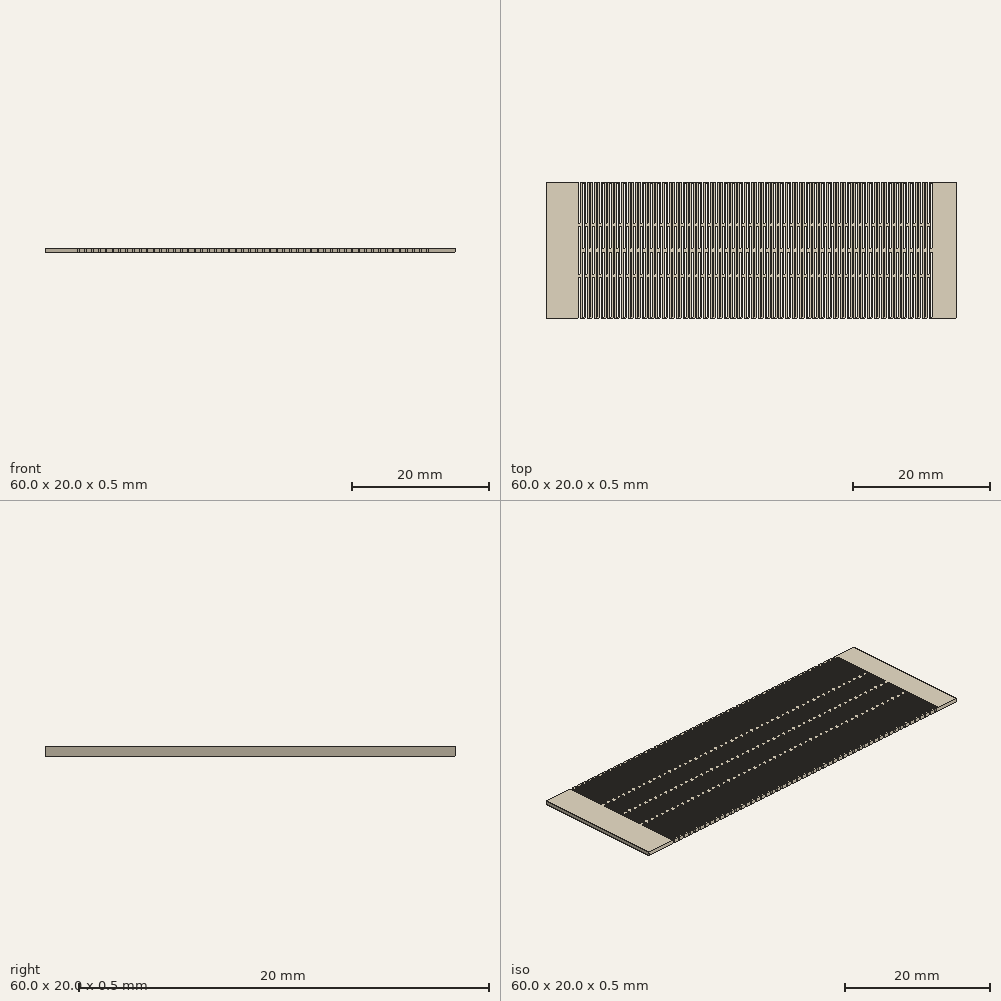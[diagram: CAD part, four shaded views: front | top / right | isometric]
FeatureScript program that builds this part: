
annotation { "Feature Type Name" : "Feature", "Feature Type Description" : "" }
export const myFeature = defineFeature(function(context is Context, id is Id, definition is map)
    precondition{}
    {
        {
            var Q0;
            Q0=qCreatedBy(makeId("Top.planeOp"),FACE);
            var sketch = newSketch(context, id + "F0", { "sketchPlane" : qUnion([Q0])});
            skLineSegment(sketch, "E0.bottom", {"start": v(30, -10) * mm, "end": v(-25, -10) * mm});
            skLineSegment(sketch, "E0.top", {"start": v(30, 10) * mm, "end": v(-24, 10) * mm});
            skLineSegment(sketch, "E0.left", {"start": v(30, -10) * mm, "end": v(30, 10) * mm});
            skLineSegment(sketch, "E0.right", {"start": v(-30, -10) * mm, "end": v(-30, 10) * mm});
            skPoint(sketch, "E0.middle", {"position": v(0, 0) * mm});
            skLineSegment(sketch, "E1", {"start": v(-25.25, 10) * mm, "end": v(-25.25, 4) * mm});
            skLineSegment(sketch, "E2", {"start": v(-25.25, 4) * mm, "end": v(-25, 4) * mm});
            skLineSegment(sketch, "E3", {"start": v(-25, 4) * mm, "end": v(-25, 10) * mm});
            skLineSegment(sketch, "E4", {"start": v(-25, 0) * mm, "end": v(-25, 3.5) * mm});
            skLineSegment(sketch, "E5", {"start": v(-25, 3.5) * mm, "end": v(-25.25, 3.5) * mm});
            skLineSegment(sketch, "E6", {"start": v(-25.25, 3.5) * mm, "end": v(-25.25, 0) * mm});
            skLineSegment(sketch, "E7", {"start": v(-24.75, 9.75) * mm, "end": v(-24.5, 9.75) * mm});
            skLineSegment(sketch, "E8", {"start": v(-24.5, 9.75) * mm, "end": v(-24.5, 0.25) * mm});
            skLineSegment(sketch, "E9", {"start": v(-24.5, 0.25) * mm, "end": v(-24.75, 0.25) * mm});
            skLineSegment(sketch, "E10", {"start": v(-24.75, 0.25) * mm, "end": v(-24.75, 9.75) * mm});
            skLineSegment(sketch, "E11.trimOffspring", {"start": v(-25.25, 10) * mm, "end": v(-30, 10) * mm});
            skLineSegment(sketch, "E12.MirrorCS", {"start": v(-25, 0) * mm, "end": v(-25, -3.5) * mm});
            skLineSegment(sketch, "E13.MirrorCS", {"start": v(-25, -3.5) * mm, "end": v(-25.25, -3.5) * mm});
            skLineSegment(sketch, "E14.MirrorCS", {"start": v(-25.25, -3.5) * mm, "end": v(-25.25, 0) * mm});
            skLineSegment(sketch, "E15.MirrorCS", {"start": v(-24.5, -0.25) * mm, "end": v(-24.75, -0.25) * mm});
            skLineSegment(sketch, "E16.MirrorCS", {"start": v(-24.75, -9.75) * mm, "end": v(-24.5, -9.75) * mm});
            skLineSegment(sketch, "E17.MirrorCS", {"start": v(-24.5, -9.75) * mm, "end": v(-24.5, -0.25) * mm});
            skLineSegment(sketch, "E18.MirrorCS", {"start": v(-24.75, -0.25) * mm, "end": v(-24.75, -9.75) * mm});
            skLineSegment(sketch, "E19.MirrorCS", {"start": v(-25, -4) * mm, "end": v(-25, -10) * mm});
            skLineSegment(sketch, "E20.MirrorCS", {"start": v(-25.25, -10) * mm, "end": v(-25.25, -4) * mm});
            skLineSegment(sketch, "E21.MirrorCS", {"start": v(-25.25, -4) * mm, "end": v(-25, -4) * mm});
            skLineSegment(sketch, "E22.trimOffspring", {"start": v(-25.25, -10) * mm, "end": v(-30, -10) * mm});
            skLineSegment(sketch, "E23.1.0.0", {"start": v(-24.25, 10) * mm, "end": v(-24.25, 4) * mm});
            skLineSegment(sketch, "E23.1.0.1", {"start": v(-24, 4) * mm, "end": v(-24, 10) * mm});
            skLineSegment(sketch, "E23.1.0.2", {"start": v(-23.75, 0.25) * mm, "end": v(-23.75, 9.75) * mm});
            skLineSegment(sketch, "E23.1.0.3", {"start": v(-23.5, 9.75) * mm, "end": v(-23.5, 0.25) * mm});
            skLineSegment(sketch, "E23.1.0.4", {"start": v(-23.75, 9.75) * mm, "end": v(-23.5, 9.75) * mm});
            skLineSegment(sketch, "E23.1.0.5", {"start": v(-24.25, 4) * mm, "end": v(-24, 4) * mm});
            skLineSegment(sketch, "E23.1.0.6", {"start": v(-23.5, 0.25) * mm, "end": v(-23.75, 0.25) * mm});
            skLineSegment(sketch, "E23.1.0.7", {"start": v(-24.25, 3.5) * mm, "end": v(-24.25, 0) * mm});
            skLineSegment(sketch, "E23.1.0.8", {"start": v(-24, 3.5) * mm, "end": v(-24.25, 3.5) * mm});
            skLineSegment(sketch, "E23.1.0.9", {"start": v(-24, 0) * mm, "end": v(-24, 3.5) * mm});
            skLineSegment(sketch, "E23.1.0.10", {"start": v(-24.25, -3.5) * mm, "end": v(-24.25, 0) * mm});
            skLineSegment(sketch, "E23.1.0.11", {"start": v(-24, -3.5) * mm, "end": v(-24.25, -3.5) * mm});
            skLineSegment(sketch, "E23.1.0.12", {"start": v(-24, 0) * mm, "end": v(-24, -3.5) * mm});
            skLineSegment(sketch, "E23.1.0.13", {"start": v(-23.75, -0.25) * mm, "end": v(-23.75, -9.75) * mm});
            skLineSegment(sketch, "E23.1.0.14", {"start": v(-23.5, -0.25) * mm, "end": v(-23.75, -0.25) * mm});
            skLineSegment(sketch, "E23.1.0.15", {"start": v(-23.5, -9.75) * mm, "end": v(-23.5, -0.25) * mm});
            skLineSegment(sketch, "E23.1.0.16", {"start": v(-23.75, -9.75) * mm, "end": v(-23.5, -9.75) * mm});
            skLineSegment(sketch, "E23.1.0.17", {"start": v(-24, -4) * mm, "end": v(-24, -10) * mm});
            skLineSegment(sketch, "E23.1.0.18", {"start": v(-24.25, -10) * mm, "end": v(-24.25, -4) * mm});
            skLineSegment(sketch, "E23.1.0.19", {"start": v(-24.25, -4) * mm, "end": v(-24, -4) * mm});
            skLineSegment(sketch, "E23.2.0.0", {"start": v(-23.25, 10) * mm, "end": v(-23.25, 4) * mm});
            skLineSegment(sketch, "E23.2.0.1", {"start": v(-23, 4) * mm, "end": v(-23, 10) * mm});
            skLineSegment(sketch, "E23.2.0.2", {"start": v(-22.75, 0.25) * mm, "end": v(-22.75, 9.75) * mm});
            skLineSegment(sketch, "E23.2.0.3", {"start": v(-22.5, 9.75) * mm, "end": v(-22.5, 0.25) * mm});
            skLineSegment(sketch, "E23.2.0.4", {"start": v(-22.75, 9.75) * mm, "end": v(-22.5, 9.75) * mm});
            skLineSegment(sketch, "E23.2.0.5", {"start": v(-23.25, 4) * mm, "end": v(-23, 4) * mm});
            skLineSegment(sketch, "E23.2.0.6", {"start": v(-22.5, 0.25) * mm, "end": v(-22.75, 0.25) * mm});
            skLineSegment(sketch, "E23.2.0.7", {"start": v(-23.25, 3.5) * mm, "end": v(-23.25, 0) * mm});
            skLineSegment(sketch, "E23.2.0.8", {"start": v(-23, 3.5) * mm, "end": v(-23.25, 3.5) * mm});
            skLineSegment(sketch, "E23.2.0.9", {"start": v(-23, 0) * mm, "end": v(-23, 3.5) * mm});
            skLineSegment(sketch, "E23.2.0.10", {"start": v(-23.25, -3.5) * mm, "end": v(-23.25, 0) * mm});
            skLineSegment(sketch, "E23.2.0.11", {"start": v(-23, -3.5) * mm, "end": v(-23.25, -3.5) * mm});
            skLineSegment(sketch, "E23.2.0.12", {"start": v(-23, 0) * mm, "end": v(-23, -3.5) * mm});
            skLineSegment(sketch, "E23.2.0.13", {"start": v(-22.75, -0.25) * mm, "end": v(-22.75, -9.75) * mm});
            skLineSegment(sketch, "E23.2.0.14", {"start": v(-22.5, -0.25) * mm, "end": v(-22.75, -0.25) * mm});
            skLineSegment(sketch, "E23.2.0.15", {"start": v(-22.5, -9.75) * mm, "end": v(-22.5, -0.25) * mm});
            skLineSegment(sketch, "E23.2.0.16", {"start": v(-22.75, -9.75) * mm, "end": v(-22.5, -9.75) * mm});
            skLineSegment(sketch, "E23.2.0.17", {"start": v(-23, -4) * mm, "end": v(-23, -10) * mm});
            skLineSegment(sketch, "E23.2.0.18", {"start": v(-23.25, -10) * mm, "end": v(-23.25, -4) * mm});
            skLineSegment(sketch, "E23.2.0.19", {"start": v(-23.25, -4) * mm, "end": v(-23, -4) * mm});
            skLineSegment(sketch, "E23.3.0.0", {"start": v(-22.25, 10) * mm, "end": v(-22.25, 4) * mm});
            skLineSegment(sketch, "E23.3.0.1", {"start": v(-22, 4) * mm, "end": v(-22, 10) * mm});
            skLineSegment(sketch, "E23.3.0.2", {"start": v(-21.75, 0.25) * mm, "end": v(-21.75, 9.75) * mm});
            skLineSegment(sketch, "E23.3.0.3", {"start": v(-21.5, 9.75) * mm, "end": v(-21.5, 0.25) * mm});
            skLineSegment(sketch, "E23.3.0.4", {"start": v(-21.75, 9.75) * mm, "end": v(-21.5, 9.75) * mm});
            skLineSegment(sketch, "E23.3.0.5", {"start": v(-22.25, 4) * mm, "end": v(-22, 4) * mm});
            skLineSegment(sketch, "E23.3.0.6", {"start": v(-21.5, 0.25) * mm, "end": v(-21.75, 0.25) * mm});
            skLineSegment(sketch, "E23.3.0.7", {"start": v(-22.25, 3.5) * mm, "end": v(-22.25, 0) * mm});
            skLineSegment(sketch, "E23.3.0.8", {"start": v(-22, 3.5) * mm, "end": v(-22.25, 3.5) * mm});
            skLineSegment(sketch, "E23.3.0.9", {"start": v(-22, 0) * mm, "end": v(-22, 3.5) * mm});
            skLineSegment(sketch, "E23.3.0.10", {"start": v(-22.25, -3.5) * mm, "end": v(-22.25, 0) * mm});
            skLineSegment(sketch, "E23.3.0.11", {"start": v(-22, -3.5) * mm, "end": v(-22.25, -3.5) * mm});
            skLineSegment(sketch, "E23.3.0.12", {"start": v(-22, 0) * mm, "end": v(-22, -3.5) * mm});
            skLineSegment(sketch, "E23.3.0.13", {"start": v(-21.75, -0.25) * mm, "end": v(-21.75, -9.75) * mm});
            skLineSegment(sketch, "E23.3.0.14", {"start": v(-21.5, -0.25) * mm, "end": v(-21.75, -0.25) * mm});
            skLineSegment(sketch, "E23.3.0.15", {"start": v(-21.5, -9.75) * mm, "end": v(-21.5, -0.25) * mm});
            skLineSegment(sketch, "E23.3.0.16", {"start": v(-21.75, -9.75) * mm, "end": v(-21.5, -9.75) * mm});
            skLineSegment(sketch, "E23.3.0.17", {"start": v(-22, -4) * mm, "end": v(-22, -10) * mm});
            skLineSegment(sketch, "E23.3.0.18", {"start": v(-22.25, -10) * mm, "end": v(-22.25, -4) * mm});
            skLineSegment(sketch, "E23.3.0.19", {"start": v(-22.25, -4) * mm, "end": v(-22, -4) * mm});
            skLineSegment(sketch, "E23.4.0.0", {"start": v(-21.25, 10) * mm, "end": v(-21.25, 4) * mm});
            skLineSegment(sketch, "E23.4.0.1", {"start": v(-21, 4) * mm, "end": v(-21, 10) * mm});
            skLineSegment(sketch, "E23.4.0.2", {"start": v(-20.75, 0.25) * mm, "end": v(-20.75, 9.75) * mm});
            skLineSegment(sketch, "E23.4.0.3", {"start": v(-20.5, 9.75) * mm, "end": v(-20.5, 0.25) * mm});
            skLineSegment(sketch, "E23.4.0.4", {"start": v(-20.75, 9.75) * mm, "end": v(-20.5, 9.75) * mm});
            skLineSegment(sketch, "E23.4.0.5", {"start": v(-21.25, 4) * mm, "end": v(-21, 4) * mm});
            skLineSegment(sketch, "E23.4.0.6", {"start": v(-20.5, 0.25) * mm, "end": v(-20.75, 0.25) * mm});
            skLineSegment(sketch, "E23.4.0.7", {"start": v(-21.25, 3.5) * mm, "end": v(-21.25, 0) * mm});
            skLineSegment(sketch, "E23.4.0.8", {"start": v(-21, 3.5) * mm, "end": v(-21.25, 3.5) * mm});
            skLineSegment(sketch, "E23.4.0.9", {"start": v(-21, 0) * mm, "end": v(-21, 3.5) * mm});
            skLineSegment(sketch, "E23.4.0.10", {"start": v(-21.25, -3.5) * mm, "end": v(-21.25, 0) * mm});
            skLineSegment(sketch, "E23.4.0.11", {"start": v(-21, -3.5) * mm, "end": v(-21.25, -3.5) * mm});
            skLineSegment(sketch, "E23.4.0.12", {"start": v(-21, 0) * mm, "end": v(-21, -3.5) * mm});
            skLineSegment(sketch, "E23.4.0.13", {"start": v(-20.75, -0.25) * mm, "end": v(-20.75, -9.75) * mm});
            skLineSegment(sketch, "E23.4.0.14", {"start": v(-20.5, -0.25) * mm, "end": v(-20.75, -0.25) * mm});
            skLineSegment(sketch, "E23.4.0.15", {"start": v(-20.5, -9.75) * mm, "end": v(-20.5, -0.25) * mm});
            skLineSegment(sketch, "E23.4.0.16", {"start": v(-20.75, -9.75) * mm, "end": v(-20.5, -9.75) * mm});
            skLineSegment(sketch, "E23.4.0.17", {"start": v(-21, -4) * mm, "end": v(-21, -10) * mm});
            skLineSegment(sketch, "E23.4.0.18", {"start": v(-21.25, -10) * mm, "end": v(-21.25, -4) * mm});
            skLineSegment(sketch, "E23.4.0.19", {"start": v(-21.25, -4) * mm, "end": v(-21, -4) * mm});
            skLineSegment(sketch, "E23.5.0.0", {"start": v(-20.25, 10) * mm, "end": v(-20.25, 4) * mm});
            skLineSegment(sketch, "E23.5.0.1", {"start": v(-20, 4) * mm, "end": v(-20, 10) * mm});
            skLineSegment(sketch, "E23.5.0.2", {"start": v(-19.75, 0.25) * mm, "end": v(-19.75, 9.75) * mm});
            skLineSegment(sketch, "E23.5.0.3", {"start": v(-19.5, 9.75) * mm, "end": v(-19.5, 0.25) * mm});
            skLineSegment(sketch, "E23.5.0.4", {"start": v(-19.75, 9.75) * mm, "end": v(-19.5, 9.75) * mm});
            skLineSegment(sketch, "E23.5.0.5", {"start": v(-20.25, 4) * mm, "end": v(-20, 4) * mm});
            skLineSegment(sketch, "E23.5.0.6", {"start": v(-19.5, 0.25) * mm, "end": v(-19.75, 0.25) * mm});
            skLineSegment(sketch, "E23.5.0.7", {"start": v(-20.25, 3.5) * mm, "end": v(-20.25, 0) * mm});
            skLineSegment(sketch, "E23.5.0.8", {"start": v(-20, 3.5) * mm, "end": v(-20.25, 3.5) * mm});
            skLineSegment(sketch, "E23.5.0.9", {"start": v(-20, 0) * mm, "end": v(-20, 3.5) * mm});
            skLineSegment(sketch, "E23.5.0.10", {"start": v(-20.25, -3.5) * mm, "end": v(-20.25, 0) * mm});
            skLineSegment(sketch, "E23.5.0.11", {"start": v(-20, -3.5) * mm, "end": v(-20.25, -3.5) * mm});
            skLineSegment(sketch, "E23.5.0.12", {"start": v(-20, 0) * mm, "end": v(-20, -3.5) * mm});
            skLineSegment(sketch, "E23.5.0.13", {"start": v(-19.75, -0.25) * mm, "end": v(-19.75, -9.75) * mm});
            skLineSegment(sketch, "E23.5.0.14", {"start": v(-19.5, -0.25) * mm, "end": v(-19.75, -0.25) * mm});
            skLineSegment(sketch, "E23.5.0.15", {"start": v(-19.5, -9.75) * mm, "end": v(-19.5, -0.25) * mm});
            skLineSegment(sketch, "E23.5.0.16", {"start": v(-19.75, -9.75) * mm, "end": v(-19.5, -9.75) * mm});
            skLineSegment(sketch, "E23.5.0.17", {"start": v(-20, -4) * mm, "end": v(-20, -10) * mm});
            skLineSegment(sketch, "E23.5.0.18", {"start": v(-20.25, -10) * mm, "end": v(-20.25, -4) * mm});
            skLineSegment(sketch, "E23.5.0.19", {"start": v(-20.25, -4) * mm, "end": v(-20, -4) * mm});
            skLineSegment(sketch, "E23.6.0.0", {"start": v(-19.25, 10) * mm, "end": v(-19.25, 4) * mm});
            skLineSegment(sketch, "E23.6.0.1", {"start": v(-19, 4) * mm, "end": v(-19, 10) * mm});
            skLineSegment(sketch, "E23.6.0.2", {"start": v(-18.75, 0.25) * mm, "end": v(-18.75, 9.75) * mm});
            skLineSegment(sketch, "E23.6.0.3", {"start": v(-18.5, 9.75) * mm, "end": v(-18.5, 0.25) * mm});
            skLineSegment(sketch, "E23.6.0.4", {"start": v(-18.75, 9.75) * mm, "end": v(-18.5, 9.75) * mm});
            skLineSegment(sketch, "E23.6.0.5", {"start": v(-19.25, 4) * mm, "end": v(-19, 4) * mm});
            skLineSegment(sketch, "E23.6.0.6", {"start": v(-18.5, 0.25) * mm, "end": v(-18.75, 0.25) * mm});
            skLineSegment(sketch, "E23.6.0.7", {"start": v(-19.25, 3.5) * mm, "end": v(-19.25, 0) * mm});
            skLineSegment(sketch, "E23.6.0.8", {"start": v(-19, 3.5) * mm, "end": v(-19.25, 3.5) * mm});
            skLineSegment(sketch, "E23.6.0.9", {"start": v(-19, 0) * mm, "end": v(-19, 3.5) * mm});
            skLineSegment(sketch, "E23.6.0.10", {"start": v(-19.25, -3.5) * mm, "end": v(-19.25, 0) * mm});
            skLineSegment(sketch, "E23.6.0.11", {"start": v(-19, -3.5) * mm, "end": v(-19.25, -3.5) * mm});
            skLineSegment(sketch, "E23.6.0.12", {"start": v(-19, 0) * mm, "end": v(-19, -3.5) * mm});
            skLineSegment(sketch, "E23.6.0.13", {"start": v(-18.75, -0.25) * mm, "end": v(-18.75, -9.75) * mm});
            skLineSegment(sketch, "E23.6.0.14", {"start": v(-18.5, -0.25) * mm, "end": v(-18.75, -0.25) * mm});
            skLineSegment(sketch, "E23.6.0.15", {"start": v(-18.5, -9.75) * mm, "end": v(-18.5, -0.25) * mm});
            skLineSegment(sketch, "E23.6.0.16", {"start": v(-18.75, -9.75) * mm, "end": v(-18.5, -9.75) * mm});
            skLineSegment(sketch, "E23.6.0.17", {"start": v(-19, -4) * mm, "end": v(-19, -10) * mm});
            skLineSegment(sketch, "E23.6.0.18", {"start": v(-19.25, -10) * mm, "end": v(-19.25, -4) * mm});
            skLineSegment(sketch, "E23.6.0.19", {"start": v(-19.25, -4) * mm, "end": v(-19, -4) * mm});
            skLineSegment(sketch, "E23.7.0.0", {"start": v(-18.25, 10) * mm, "end": v(-18.25, 4) * mm});
            skLineSegment(sketch, "E23.7.0.1", {"start": v(-18, 4) * mm, "end": v(-18, 10) * mm});
            skLineSegment(sketch, "E23.7.0.2", {"start": v(-17.75, 0.25) * mm, "end": v(-17.75, 9.75) * mm});
            skLineSegment(sketch, "E23.7.0.3", {"start": v(-17.5, 9.75) * mm, "end": v(-17.5, 0.25) * mm});
            skLineSegment(sketch, "E23.7.0.4", {"start": v(-17.75, 9.75) * mm, "end": v(-17.5, 9.75) * mm});
            skLineSegment(sketch, "E23.7.0.5", {"start": v(-18.25, 4) * mm, "end": v(-18, 4) * mm});
            skLineSegment(sketch, "E23.7.0.6", {"start": v(-17.5, 0.25) * mm, "end": v(-17.75, 0.25) * mm});
            skLineSegment(sketch, "E23.7.0.7", {"start": v(-18.25, 3.5) * mm, "end": v(-18.25, 0) * mm});
            skLineSegment(sketch, "E23.7.0.8", {"start": v(-18, 3.5) * mm, "end": v(-18.25, 3.5) * mm});
            skLineSegment(sketch, "E23.7.0.9", {"start": v(-18, 0) * mm, "end": v(-18, 3.5) * mm});
            skLineSegment(sketch, "E23.7.0.10", {"start": v(-18.25, -3.5) * mm, "end": v(-18.25, 0) * mm});
            skLineSegment(sketch, "E23.7.0.11", {"start": v(-18, -3.5) * mm, "end": v(-18.25, -3.5) * mm});
            skLineSegment(sketch, "E23.7.0.12", {"start": v(-18, 0) * mm, "end": v(-18, -3.5) * mm});
            skLineSegment(sketch, "E23.7.0.13", {"start": v(-17.75, -0.25) * mm, "end": v(-17.75, -9.75) * mm});
            skLineSegment(sketch, "E23.7.0.14", {"start": v(-17.5, -0.25) * mm, "end": v(-17.75, -0.25) * mm});
            skLineSegment(sketch, "E23.7.0.15", {"start": v(-17.5, -9.75) * mm, "end": v(-17.5, -0.25) * mm});
            skLineSegment(sketch, "E23.7.0.16", {"start": v(-17.75, -9.75) * mm, "end": v(-17.5, -9.75) * mm});
            skLineSegment(sketch, "E23.7.0.17", {"start": v(-18, -4) * mm, "end": v(-18, -10) * mm});
            skLineSegment(sketch, "E23.7.0.18", {"start": v(-18.25, -10) * mm, "end": v(-18.25, -4) * mm});
            skLineSegment(sketch, "E23.7.0.19", {"start": v(-18.25, -4) * mm, "end": v(-18, -4) * mm});
            skLineSegment(sketch, "E23.8.0.0", {"start": v(-17.25, 10) * mm, "end": v(-17.25, 4) * mm});
            skLineSegment(sketch, "E23.8.0.1", {"start": v(-17, 4) * mm, "end": v(-17, 10) * mm});
            skLineSegment(sketch, "E23.8.0.2", {"start": v(-16.75, 0.25) * mm, "end": v(-16.75, 9.75) * mm});
            skLineSegment(sketch, "E23.8.0.3", {"start": v(-16.5, 9.75) * mm, "end": v(-16.5, 0.25) * mm});
            skLineSegment(sketch, "E23.8.0.4", {"start": v(-16.75, 9.75) * mm, "end": v(-16.5, 9.75) * mm});
            skLineSegment(sketch, "E23.8.0.5", {"start": v(-17.25, 4) * mm, "end": v(-17, 4) * mm});
            skLineSegment(sketch, "E23.8.0.6", {"start": v(-16.5, 0.25) * mm, "end": v(-16.75, 0.25) * mm});
            skLineSegment(sketch, "E23.8.0.7", {"start": v(-17.25, 3.5) * mm, "end": v(-17.25, 0) * mm});
            skLineSegment(sketch, "E23.8.0.8", {"start": v(-17, 3.5) * mm, "end": v(-17.25, 3.5) * mm});
            skLineSegment(sketch, "E23.8.0.9", {"start": v(-17, 0) * mm, "end": v(-17, 3.5) * mm});
            skLineSegment(sketch, "E23.8.0.10", {"start": v(-17.25, -3.5) * mm, "end": v(-17.25, 0) * mm});
            skLineSegment(sketch, "E23.8.0.11", {"start": v(-17, -3.5) * mm, "end": v(-17.25, -3.5) * mm});
            skLineSegment(sketch, "E23.8.0.12", {"start": v(-17, 0) * mm, "end": v(-17, -3.5) * mm});
            skLineSegment(sketch, "E23.8.0.13", {"start": v(-16.75, -0.25) * mm, "end": v(-16.75, -9.75) * mm});
            skLineSegment(sketch, "E23.8.0.14", {"start": v(-16.5, -0.25) * mm, "end": v(-16.75, -0.25) * mm});
            skLineSegment(sketch, "E23.8.0.15", {"start": v(-16.5, -9.75) * mm, "end": v(-16.5, -0.25) * mm});
            skLineSegment(sketch, "E23.8.0.16", {"start": v(-16.75, -9.75) * mm, "end": v(-16.5, -9.75) * mm});
            skLineSegment(sketch, "E23.8.0.17", {"start": v(-17, -4) * mm, "end": v(-17, -10) * mm});
            skLineSegment(sketch, "E23.8.0.18", {"start": v(-17.25, -10) * mm, "end": v(-17.25, -4) * mm});
            skLineSegment(sketch, "E23.8.0.19", {"start": v(-17.25, -4) * mm, "end": v(-17, -4) * mm});
            skLineSegment(sketch, "E23.9.0.0", {"start": v(-16.25, 10) * mm, "end": v(-16.25, 4) * mm});
            skLineSegment(sketch, "E23.9.0.1", {"start": v(-16, 4) * mm, "end": v(-16, 10) * mm});
            skLineSegment(sketch, "E23.9.0.2", {"start": v(-15.75, 0.25) * mm, "end": v(-15.75, 9.75) * mm});
            skLineSegment(sketch, "E23.9.0.3", {"start": v(-15.5, 9.75) * mm, "end": v(-15.5, 0.25) * mm});
            skLineSegment(sketch, "E23.9.0.4", {"start": v(-15.75, 9.75) * mm, "end": v(-15.5, 9.75) * mm});
            skLineSegment(sketch, "E23.9.0.5", {"start": v(-16.25, 4) * mm, "end": v(-16, 4) * mm});
            skLineSegment(sketch, "E23.9.0.6", {"start": v(-15.5, 0.25) * mm, "end": v(-15.75, 0.25) * mm});
            skLineSegment(sketch, "E23.9.0.7", {"start": v(-16.25, 3.5) * mm, "end": v(-16.25, 0) * mm});
            skLineSegment(sketch, "E23.9.0.8", {"start": v(-16, 3.5) * mm, "end": v(-16.25, 3.5) * mm});
            skLineSegment(sketch, "E23.9.0.9", {"start": v(-16, 0) * mm, "end": v(-16, 3.5) * mm});
            skLineSegment(sketch, "E23.9.0.10", {"start": v(-16.25, -3.5) * mm, "end": v(-16.25, 0) * mm});
            skLineSegment(sketch, "E23.9.0.11", {"start": v(-16, -3.5) * mm, "end": v(-16.25, -3.5) * mm});
            skLineSegment(sketch, "E23.9.0.12", {"start": v(-16, 0) * mm, "end": v(-16, -3.5) * mm});
            skLineSegment(sketch, "E23.9.0.13", {"start": v(-15.75, -0.25) * mm, "end": v(-15.75, -9.75) * mm});
            skLineSegment(sketch, "E23.9.0.14", {"start": v(-15.5, -0.25) * mm, "end": v(-15.75, -0.25) * mm});
            skLineSegment(sketch, "E23.9.0.15", {"start": v(-15.5, -9.75) * mm, "end": v(-15.5, -0.25) * mm});
            skLineSegment(sketch, "E23.9.0.16", {"start": v(-15.75, -9.75) * mm, "end": v(-15.5, -9.75) * mm});
            skLineSegment(sketch, "E23.9.0.17", {"start": v(-16, -4) * mm, "end": v(-16, -10) * mm});
            skLineSegment(sketch, "E23.9.0.18", {"start": v(-16.25, -10) * mm, "end": v(-16.25, -4) * mm});
            skLineSegment(sketch, "E23.9.0.19", {"start": v(-16.25, -4) * mm, "end": v(-16, -4) * mm});
            skLineSegment(sketch, "E23.10.0.0", {"start": v(-15.25, 10) * mm, "end": v(-15.25, 4) * mm});
            skLineSegment(sketch, "E23.10.0.1", {"start": v(-15, 4) * mm, "end": v(-15, 10) * mm});
            skLineSegment(sketch, "E23.10.0.2", {"start": v(-14.75, 0.25) * mm, "end": v(-14.75, 9.75) * mm});
            skLineSegment(sketch, "E23.10.0.3", {"start": v(-14.5, 9.75) * mm, "end": v(-14.5, 0.25) * mm});
            skLineSegment(sketch, "E23.10.0.4", {"start": v(-14.75, 9.75) * mm, "end": v(-14.5, 9.75) * mm});
            skLineSegment(sketch, "E23.10.0.5", {"start": v(-15.25, 4) * mm, "end": v(-15, 4) * mm});
            skLineSegment(sketch, "E23.10.0.6", {"start": v(-14.5, 0.25) * mm, "end": v(-14.75, 0.25) * mm});
            skLineSegment(sketch, "E23.10.0.7", {"start": v(-15.25, 3.5) * mm, "end": v(-15.25, 0) * mm});
            skLineSegment(sketch, "E23.10.0.8", {"start": v(-15, 3.5) * mm, "end": v(-15.25, 3.5) * mm});
            skLineSegment(sketch, "E23.10.0.9", {"start": v(-15, 0) * mm, "end": v(-15, 3.5) * mm});
            skLineSegment(sketch, "E23.10.0.10", {"start": v(-15.25, -3.5) * mm, "end": v(-15.25, 0) * mm});
            skLineSegment(sketch, "E23.10.0.11", {"start": v(-15, -3.5) * mm, "end": v(-15.25, -3.5) * mm});
            skLineSegment(sketch, "E23.10.0.12", {"start": v(-15, 0) * mm, "end": v(-15, -3.5) * mm});
            skLineSegment(sketch, "E23.10.0.13", {"start": v(-14.75, -0.25) * mm, "end": v(-14.75, -9.75) * mm});
            skLineSegment(sketch, "E23.10.0.14", {"start": v(-14.5, -0.25) * mm, "end": v(-14.75, -0.25) * mm});
            skLineSegment(sketch, "E23.10.0.15", {"start": v(-14.5, -9.75) * mm, "end": v(-14.5, -0.25) * mm});
            skLineSegment(sketch, "E23.10.0.16", {"start": v(-14.75, -9.75) * mm, "end": v(-14.5, -9.75) * mm});
            skLineSegment(sketch, "E23.10.0.17", {"start": v(-15, -4) * mm, "end": v(-15, -10) * mm});
            skLineSegment(sketch, "E23.10.0.18", {"start": v(-15.25, -10) * mm, "end": v(-15.25, -4) * mm});
            skLineSegment(sketch, "E23.10.0.19", {"start": v(-15.25, -4) * mm, "end": v(-15, -4) * mm});
            skLineSegment(sketch, "E23.11.0.0", {"start": v(-14.25, 10) * mm, "end": v(-14.25, 4) * mm});
            skLineSegment(sketch, "E23.11.0.1", {"start": v(-14, 4) * mm, "end": v(-14, 10) * mm});
            skLineSegment(sketch, "E23.11.0.2", {"start": v(-13.75, 0.25) * mm, "end": v(-13.75, 9.75) * mm});
            skLineSegment(sketch, "E23.11.0.3", {"start": v(-13.5, 9.75) * mm, "end": v(-13.5, 0.25) * mm});
            skLineSegment(sketch, "E23.11.0.4", {"start": v(-13.75, 9.75) * mm, "end": v(-13.5, 9.75) * mm});
            skLineSegment(sketch, "E23.11.0.5", {"start": v(-14.25, 4) * mm, "end": v(-14, 4) * mm});
            skLineSegment(sketch, "E23.11.0.6", {"start": v(-13.5, 0.25) * mm, "end": v(-13.75, 0.25) * mm});
            skLineSegment(sketch, "E23.11.0.7", {"start": v(-14.25, 3.5) * mm, "end": v(-14.25, 0) * mm});
            skLineSegment(sketch, "E23.11.0.8", {"start": v(-14, 3.5) * mm, "end": v(-14.25, 3.5) * mm});
            skLineSegment(sketch, "E23.11.0.9", {"start": v(-14, 0) * mm, "end": v(-14, 3.5) * mm});
            skLineSegment(sketch, "E23.11.0.10", {"start": v(-14.25, -3.5) * mm, "end": v(-14.25, 0) * mm});
            skLineSegment(sketch, "E23.11.0.11", {"start": v(-14, -3.5) * mm, "end": v(-14.25, -3.5) * mm});
            skLineSegment(sketch, "E23.11.0.12", {"start": v(-14, 0) * mm, "end": v(-14, -3.5) * mm});
            skLineSegment(sketch, "E23.11.0.13", {"start": v(-13.75, -0.25) * mm, "end": v(-13.75, -9.75) * mm});
            skLineSegment(sketch, "E23.11.0.14", {"start": v(-13.5, -0.25) * mm, "end": v(-13.75, -0.25) * mm});
            skLineSegment(sketch, "E23.11.0.15", {"start": v(-13.5, -9.75) * mm, "end": v(-13.5, -0.25) * mm});
            skLineSegment(sketch, "E23.11.0.16", {"start": v(-13.75, -9.75) * mm, "end": v(-13.5, -9.75) * mm});
            skLineSegment(sketch, "E23.11.0.17", {"start": v(-14, -4) * mm, "end": v(-14, -10) * mm});
            skLineSegment(sketch, "E23.11.0.18", {"start": v(-14.25, -10) * mm, "end": v(-14.25, -4) * mm});
            skLineSegment(sketch, "E23.11.0.19", {"start": v(-14.25, -4) * mm, "end": v(-14, -4) * mm});
            skLineSegment(sketch, "E23.12.0.0", {"start": v(-13.25, 10) * mm, "end": v(-13.25, 4) * mm});
            skLineSegment(sketch, "E23.12.0.1", {"start": v(-13, 4) * mm, "end": v(-13, 10) * mm});
            skLineSegment(sketch, "E23.12.0.2", {"start": v(-12.75, 0.25) * mm, "end": v(-12.75, 9.75) * mm});
            skLineSegment(sketch, "E23.12.0.3", {"start": v(-12.5, 9.75) * mm, "end": v(-12.5, 0.25) * mm});
            skLineSegment(sketch, "E23.12.0.4", {"start": v(-12.75, 9.75) * mm, "end": v(-12.5, 9.75) * mm});
            skLineSegment(sketch, "E23.12.0.5", {"start": v(-13.25, 4) * mm, "end": v(-13, 4) * mm});
            skLineSegment(sketch, "E23.12.0.6", {"start": v(-12.5, 0.25) * mm, "end": v(-12.75, 0.25) * mm});
            skLineSegment(sketch, "E23.12.0.7", {"start": v(-13.25, 3.5) * mm, "end": v(-13.25, 0) * mm});
            skLineSegment(sketch, "E23.12.0.8", {"start": v(-13, 3.5) * mm, "end": v(-13.25, 3.5) * mm});
            skLineSegment(sketch, "E23.12.0.9", {"start": v(-13, 0) * mm, "end": v(-13, 3.5) * mm});
            skLineSegment(sketch, "E23.12.0.10", {"start": v(-13.25, -3.5) * mm, "end": v(-13.25, 0) * mm});
            skLineSegment(sketch, "E23.12.0.11", {"start": v(-13, -3.5) * mm, "end": v(-13.25, -3.5) * mm});
            skLineSegment(sketch, "E23.12.0.12", {"start": v(-13, 0) * mm, "end": v(-13, -3.5) * mm});
            skLineSegment(sketch, "E23.12.0.13", {"start": v(-12.75, -0.25) * mm, "end": v(-12.75, -9.75) * mm});
            skLineSegment(sketch, "E23.12.0.14", {"start": v(-12.5, -0.25) * mm, "end": v(-12.75, -0.25) * mm});
            skLineSegment(sketch, "E23.12.0.15", {"start": v(-12.5, -9.75) * mm, "end": v(-12.5, -0.25) * mm});
            skLineSegment(sketch, "E23.12.0.16", {"start": v(-12.75, -9.75) * mm, "end": v(-12.5, -9.75) * mm});
            skLineSegment(sketch, "E23.12.0.17", {"start": v(-13, -4) * mm, "end": v(-13, -10) * mm});
            skLineSegment(sketch, "E23.12.0.18", {"start": v(-13.25, -10) * mm, "end": v(-13.25, -4) * mm});
            skLineSegment(sketch, "E23.12.0.19", {"start": v(-13.25, -4) * mm, "end": v(-13, -4) * mm});
            skLineSegment(sketch, "E23.13.0.0", {"start": v(-12.25, 10) * mm, "end": v(-12.25, 4) * mm});
            skLineSegment(sketch, "E23.13.0.1", {"start": v(-12, 4) * mm, "end": v(-12, 10) * mm});
            skLineSegment(sketch, "E23.13.0.2", {"start": v(-11.75, 0.25) * mm, "end": v(-11.75, 9.75) * mm});
            skLineSegment(sketch, "E23.13.0.3", {"start": v(-11.5, 9.75) * mm, "end": v(-11.5, 0.25) * mm});
            skLineSegment(sketch, "E23.13.0.4", {"start": v(-11.75, 9.75) * mm, "end": v(-11.5, 9.75) * mm});
            skLineSegment(sketch, "E23.13.0.5", {"start": v(-12.25, 4) * mm, "end": v(-12, 4) * mm});
            skLineSegment(sketch, "E23.13.0.6", {"start": v(-11.5, 0.25) * mm, "end": v(-11.75, 0.25) * mm});
            skLineSegment(sketch, "E23.13.0.7", {"start": v(-12.25, 3.5) * mm, "end": v(-12.25, 0) * mm});
            skLineSegment(sketch, "E23.13.0.8", {"start": v(-12, 3.5) * mm, "end": v(-12.25, 3.5) * mm});
            skLineSegment(sketch, "E23.13.0.9", {"start": v(-12, 0) * mm, "end": v(-12, 3.5) * mm});
            skLineSegment(sketch, "E23.13.0.10", {"start": v(-12.25, -3.5) * mm, "end": v(-12.25, 0) * mm});
            skLineSegment(sketch, "E23.13.0.11", {"start": v(-12, -3.5) * mm, "end": v(-12.25, -3.5) * mm});
            skLineSegment(sketch, "E23.13.0.12", {"start": v(-12, 0) * mm, "end": v(-12, -3.5) * mm});
            skLineSegment(sketch, "E23.13.0.13", {"start": v(-11.75, -0.25) * mm, "end": v(-11.75, -9.75) * mm});
            skLineSegment(sketch, "E23.13.0.14", {"start": v(-11.5, -0.25) * mm, "end": v(-11.75, -0.25) * mm});
            skLineSegment(sketch, "E23.13.0.15", {"start": v(-11.5, -9.75) * mm, "end": v(-11.5, -0.25) * mm});
            skLineSegment(sketch, "E23.13.0.16", {"start": v(-11.75, -9.75) * mm, "end": v(-11.5, -9.75) * mm});
            skLineSegment(sketch, "E23.13.0.17", {"start": v(-12, -4) * mm, "end": v(-12, -10) * mm});
            skLineSegment(sketch, "E23.13.0.18", {"start": v(-12.25, -10) * mm, "end": v(-12.25, -4) * mm});
            skLineSegment(sketch, "E23.13.0.19", {"start": v(-12.25, -4) * mm, "end": v(-12, -4) * mm});
            skLineSegment(sketch, "E23.14.0.0", {"start": v(-11.25, 10) * mm, "end": v(-11.25, 4) * mm});
            skLineSegment(sketch, "E23.14.0.1", {"start": v(-11, 4) * mm, "end": v(-11, 10) * mm});
            skLineSegment(sketch, "E23.14.0.2", {"start": v(-10.75, 0.25) * mm, "end": v(-10.75, 9.75) * mm});
            skLineSegment(sketch, "E23.14.0.3", {"start": v(-10.5, 9.75) * mm, "end": v(-10.5, 0.25) * mm});
            skLineSegment(sketch, "E23.14.0.4", {"start": v(-10.75, 9.75) * mm, "end": v(-10.5, 9.75) * mm});
            skLineSegment(sketch, "E23.14.0.5", {"start": v(-11.25, 4) * mm, "end": v(-11, 4) * mm});
            skLineSegment(sketch, "E23.14.0.6", {"start": v(-10.5, 0.25) * mm, "end": v(-10.75, 0.25) * mm});
            skLineSegment(sketch, "E23.14.0.7", {"start": v(-11.25, 3.5) * mm, "end": v(-11.25, 0) * mm});
            skLineSegment(sketch, "E23.14.0.8", {"start": v(-11, 3.5) * mm, "end": v(-11.25, 3.5) * mm});
            skLineSegment(sketch, "E23.14.0.9", {"start": v(-11, 0) * mm, "end": v(-11, 3.5) * mm});
            skLineSegment(sketch, "E23.14.0.10", {"start": v(-11.25, -3.5) * mm, "end": v(-11.25, 0) * mm});
            skLineSegment(sketch, "E23.14.0.11", {"start": v(-11, -3.5) * mm, "end": v(-11.25, -3.5) * mm});
            skLineSegment(sketch, "E23.14.0.12", {"start": v(-11, 0) * mm, "end": v(-11, -3.5) * mm});
            skLineSegment(sketch, "E23.14.0.13", {"start": v(-10.75, -0.25) * mm, "end": v(-10.75, -9.75) * mm});
            skLineSegment(sketch, "E23.14.0.14", {"start": v(-10.5, -0.25) * mm, "end": v(-10.75, -0.25) * mm});
            skLineSegment(sketch, "E23.14.0.15", {"start": v(-10.5, -9.75) * mm, "end": v(-10.5, -0.25) * mm});
            skLineSegment(sketch, "E23.14.0.16", {"start": v(-10.75, -9.75) * mm, "end": v(-10.5, -9.75) * mm});
            skLineSegment(sketch, "E23.14.0.17", {"start": v(-11, -4) * mm, "end": v(-11, -10) * mm});
            skLineSegment(sketch, "E23.14.0.18", {"start": v(-11.25, -10) * mm, "end": v(-11.25, -4) * mm});
            skLineSegment(sketch, "E23.14.0.19", {"start": v(-11.25, -4) * mm, "end": v(-11, -4) * mm});
            skLineSegment(sketch, "E23.15.0.0", {"start": v(-10.25, 10) * mm, "end": v(-10.25, 4) * mm});
            skLineSegment(sketch, "E23.15.0.1", {"start": v(-10, 4) * mm, "end": v(-10, 10) * mm});
            skLineSegment(sketch, "E23.15.0.2", {"start": v(-9.75, 0.25) * mm, "end": v(-9.75, 9.75) * mm});
            skLineSegment(sketch, "E23.15.0.3", {"start": v(-9.5, 9.75) * mm, "end": v(-9.5, 0.25) * mm});
            skLineSegment(sketch, "E23.15.0.4", {"start": v(-9.75, 9.75) * mm, "end": v(-9.5, 9.75) * mm});
            skLineSegment(sketch, "E23.15.0.5", {"start": v(-10.25, 4) * mm, "end": v(-10, 4) * mm});
            skLineSegment(sketch, "E23.15.0.6", {"start": v(-9.5, 0.25) * mm, "end": v(-9.75, 0.25) * mm});
            skLineSegment(sketch, "E23.15.0.7", {"start": v(-10.25, 3.5) * mm, "end": v(-10.25, 0) * mm});
            skLineSegment(sketch, "E23.15.0.8", {"start": v(-10, 3.5) * mm, "end": v(-10.25, 3.5) * mm});
            skLineSegment(sketch, "E23.15.0.9", {"start": v(-10, 0) * mm, "end": v(-10, 3.5) * mm});
            skLineSegment(sketch, "E23.15.0.10", {"start": v(-10.25, -3.5) * mm, "end": v(-10.25, 0) * mm});
            skLineSegment(sketch, "E23.15.0.11", {"start": v(-10, -3.5) * mm, "end": v(-10.25, -3.5) * mm});
            skLineSegment(sketch, "E23.15.0.12", {"start": v(-10, 0) * mm, "end": v(-10, -3.5) * mm});
            skLineSegment(sketch, "E23.15.0.13", {"start": v(-9.75, -0.25) * mm, "end": v(-9.75, -9.75) * mm});
            skLineSegment(sketch, "E23.15.0.14", {"start": v(-9.5, -0.25) * mm, "end": v(-9.75, -0.25) * mm});
            skLineSegment(sketch, "E23.15.0.15", {"start": v(-9.5, -9.75) * mm, "end": v(-9.5, -0.25) * mm});
            skLineSegment(sketch, "E23.15.0.16", {"start": v(-9.75, -9.75) * mm, "end": v(-9.5, -9.75) * mm});
            skLineSegment(sketch, "E23.15.0.17", {"start": v(-10, -4) * mm, "end": v(-10, -10) * mm});
            skLineSegment(sketch, "E23.15.0.18", {"start": v(-10.25, -10) * mm, "end": v(-10.25, -4) * mm});
            skLineSegment(sketch, "E23.15.0.19", {"start": v(-10.25, -4) * mm, "end": v(-10, -4) * mm});
            skLineSegment(sketch, "E23.16.0.0", {"start": v(-9.25, 10) * mm, "end": v(-9.25, 4) * mm});
            skLineSegment(sketch, "E23.16.0.1", {"start": v(-9, 4) * mm, "end": v(-9, 10) * mm});
            skLineSegment(sketch, "E23.16.0.2", {"start": v(-8.75, 0.25) * mm, "end": v(-8.75, 9.75) * mm});
            skLineSegment(sketch, "E23.16.0.3", {"start": v(-8.5, 9.75) * mm, "end": v(-8.5, 0.25) * mm});
            skLineSegment(sketch, "E23.16.0.4", {"start": v(-8.75, 9.75) * mm, "end": v(-8.5, 9.75) * mm});
            skLineSegment(sketch, "E23.16.0.5", {"start": v(-9.25, 4) * mm, "end": v(-9, 4) * mm});
            skLineSegment(sketch, "E23.16.0.6", {"start": v(-8.5, 0.25) * mm, "end": v(-8.75, 0.25) * mm});
            skLineSegment(sketch, "E23.16.0.7", {"start": v(-9.25, 3.5) * mm, "end": v(-9.25, 0) * mm});
            skLineSegment(sketch, "E23.16.0.8", {"start": v(-9, 3.5) * mm, "end": v(-9.25, 3.5) * mm});
            skLineSegment(sketch, "E23.16.0.9", {"start": v(-9, 0) * mm, "end": v(-9, 3.5) * mm});
            skLineSegment(sketch, "E23.16.0.10", {"start": v(-9.25, -3.5) * mm, "end": v(-9.25, 0) * mm});
            skLineSegment(sketch, "E23.16.0.11", {"start": v(-9, -3.5) * mm, "end": v(-9.25, -3.5) * mm});
            skLineSegment(sketch, "E23.16.0.12", {"start": v(-9, 0) * mm, "end": v(-9, -3.5) * mm});
            skLineSegment(sketch, "E23.16.0.13", {"start": v(-8.75, -0.25) * mm, "end": v(-8.75, -9.75) * mm});
            skLineSegment(sketch, "E23.16.0.14", {"start": v(-8.5, -0.25) * mm, "end": v(-8.75, -0.25) * mm});
            skLineSegment(sketch, "E23.16.0.15", {"start": v(-8.5, -9.75) * mm, "end": v(-8.5, -0.25) * mm});
            skLineSegment(sketch, "E23.16.0.16", {"start": v(-8.75, -9.75) * mm, "end": v(-8.5, -9.75) * mm});
            skLineSegment(sketch, "E23.16.0.17", {"start": v(-9, -4) * mm, "end": v(-9, -10) * mm});
            skLineSegment(sketch, "E23.16.0.18", {"start": v(-9.25, -10) * mm, "end": v(-9.25, -4) * mm});
            skLineSegment(sketch, "E23.16.0.19", {"start": v(-9.25, -4) * mm, "end": v(-9, -4) * mm});
            skLineSegment(sketch, "E23.17.0.0", {"start": v(-8.25, 10) * mm, "end": v(-8.25, 4) * mm});
            skLineSegment(sketch, "E23.17.0.1", {"start": v(-8, 4) * mm, "end": v(-8, 10) * mm});
            skLineSegment(sketch, "E23.17.0.2", {"start": v(-7.75, 0.25) * mm, "end": v(-7.75, 9.75) * mm});
            skLineSegment(sketch, "E23.17.0.3", {"start": v(-7.5, 9.75) * mm, "end": v(-7.5, 0.25) * mm});
            skLineSegment(sketch, "E23.17.0.4", {"start": v(-7.75, 9.75) * mm, "end": v(-7.5, 9.75) * mm});
            skLineSegment(sketch, "E23.17.0.5", {"start": v(-8.25, 4) * mm, "end": v(-8, 4) * mm});
            skLineSegment(sketch, "E23.17.0.6", {"start": v(-7.5, 0.25) * mm, "end": v(-7.75, 0.25) * mm});
            skLineSegment(sketch, "E23.17.0.7", {"start": v(-8.25, 3.5) * mm, "end": v(-8.25, 0) * mm});
            skLineSegment(sketch, "E23.17.0.8", {"start": v(-8, 3.5) * mm, "end": v(-8.25, 3.5) * mm});
            skLineSegment(sketch, "E23.17.0.9", {"start": v(-8, 0) * mm, "end": v(-8, 3.5) * mm});
            skLineSegment(sketch, "E23.17.0.10", {"start": v(-8.25, -3.5) * mm, "end": v(-8.25, 0) * mm});
            skLineSegment(sketch, "E23.17.0.11", {"start": v(-8, -3.5) * mm, "end": v(-8.25, -3.5) * mm});
            skLineSegment(sketch, "E23.17.0.12", {"start": v(-8, 0) * mm, "end": v(-8, -3.5) * mm});
            skLineSegment(sketch, "E23.17.0.13", {"start": v(-7.75, -0.25) * mm, "end": v(-7.75, -9.75) * mm});
            skLineSegment(sketch, "E23.17.0.14", {"start": v(-7.5, -0.25) * mm, "end": v(-7.75, -0.25) * mm});
            skLineSegment(sketch, "E23.17.0.15", {"start": v(-7.5, -9.75) * mm, "end": v(-7.5, -0.25) * mm});
            skLineSegment(sketch, "E23.17.0.16", {"start": v(-7.75, -9.75) * mm, "end": v(-7.5, -9.75) * mm});
            skLineSegment(sketch, "E23.17.0.17", {"start": v(-8, -4) * mm, "end": v(-8, -10) * mm});
            skLineSegment(sketch, "E23.17.0.18", {"start": v(-8.25, -10) * mm, "end": v(-8.25, -4) * mm});
            skLineSegment(sketch, "E23.17.0.19", {"start": v(-8.25, -4) * mm, "end": v(-8, -4) * mm});
            skLineSegment(sketch, "E23.18.0.0", {"start": v(-7.25, 10) * mm, "end": v(-7.25, 4) * mm});
            skLineSegment(sketch, "E23.18.0.1", {"start": v(-7, 4) * mm, "end": v(-7, 10) * mm});
            skLineSegment(sketch, "E23.18.0.2", {"start": v(-6.75, 0.25) * mm, "end": v(-6.75, 9.75) * mm});
            skLineSegment(sketch, "E23.18.0.3", {"start": v(-6.5, 9.75) * mm, "end": v(-6.5, 0.25) * mm});
            skLineSegment(sketch, "E23.18.0.4", {"start": v(-6.75, 9.75) * mm, "end": v(-6.5, 9.75) * mm});
            skLineSegment(sketch, "E23.18.0.5", {"start": v(-7.25, 4) * mm, "end": v(-7, 4) * mm});
            skLineSegment(sketch, "E23.18.0.6", {"start": v(-6.5, 0.25) * mm, "end": v(-6.75, 0.25) * mm});
            skLineSegment(sketch, "E23.18.0.7", {"start": v(-7.25, 3.5) * mm, "end": v(-7.25, 0) * mm});
            skLineSegment(sketch, "E23.18.0.8", {"start": v(-7, 3.5) * mm, "end": v(-7.25, 3.5) * mm});
            skLineSegment(sketch, "E23.18.0.9", {"start": v(-7, 0) * mm, "end": v(-7, 3.5) * mm});
            skLineSegment(sketch, "E23.18.0.10", {"start": v(-7.25, -3.5) * mm, "end": v(-7.25, 0) * mm});
            skLineSegment(sketch, "E23.18.0.11", {"start": v(-7, -3.5) * mm, "end": v(-7.25, -3.5) * mm});
            skLineSegment(sketch, "E23.18.0.12", {"start": v(-7, 0) * mm, "end": v(-7, -3.5) * mm});
            skLineSegment(sketch, "E23.18.0.13", {"start": v(-6.75, -0.25) * mm, "end": v(-6.75, -9.75) * mm});
            skLineSegment(sketch, "E23.18.0.14", {"start": v(-6.5, -0.25) * mm, "end": v(-6.75, -0.25) * mm});
            skLineSegment(sketch, "E23.18.0.15", {"start": v(-6.5, -9.75) * mm, "end": v(-6.5, -0.25) * mm});
            skLineSegment(sketch, "E23.18.0.16", {"start": v(-6.75, -9.75) * mm, "end": v(-6.5, -9.75) * mm});
            skLineSegment(sketch, "E23.18.0.17", {"start": v(-7, -4) * mm, "end": v(-7, -10) * mm});
            skLineSegment(sketch, "E23.18.0.18", {"start": v(-7.25, -10) * mm, "end": v(-7.25, -4) * mm});
            skLineSegment(sketch, "E23.18.0.19", {"start": v(-7.25, -4) * mm, "end": v(-7, -4) * mm});
            skLineSegment(sketch, "E23.19.0.0", {"start": v(-6.25, 10) * mm, "end": v(-6.25, 4) * mm});
            skLineSegment(sketch, "E23.19.0.1", {"start": v(-6, 4) * mm, "end": v(-6, 10) * mm});
            skLineSegment(sketch, "E23.19.0.2", {"start": v(-5.75, 0.25) * mm, "end": v(-5.75, 9.75) * mm});
            skLineSegment(sketch, "E23.19.0.3", {"start": v(-5.5, 9.75) * mm, "end": v(-5.5, 0.25) * mm});
            skLineSegment(sketch, "E23.19.0.4", {"start": v(-5.75, 9.75) * mm, "end": v(-5.5, 9.75) * mm});
            skLineSegment(sketch, "E23.19.0.5", {"start": v(-6.25, 4) * mm, "end": v(-6, 4) * mm});
            skLineSegment(sketch, "E23.19.0.6", {"start": v(-5.5, 0.25) * mm, "end": v(-5.75, 0.25) * mm});
            skLineSegment(sketch, "E23.19.0.7", {"start": v(-6.25, 3.5) * mm, "end": v(-6.25, 0) * mm});
            skLineSegment(sketch, "E23.19.0.8", {"start": v(-6, 3.5) * mm, "end": v(-6.25, 3.5) * mm});
            skLineSegment(sketch, "E23.19.0.9", {"start": v(-6, 0) * mm, "end": v(-6, 3.5) * mm});
            skLineSegment(sketch, "E23.19.0.10", {"start": v(-6.25, -3.5) * mm, "end": v(-6.25, 0) * mm});
            skLineSegment(sketch, "E23.19.0.11", {"start": v(-6, -3.5) * mm, "end": v(-6.25, -3.5) * mm});
            skLineSegment(sketch, "E23.19.0.12", {"start": v(-6, 0) * mm, "end": v(-6, -3.5) * mm});
            skLineSegment(sketch, "E23.19.0.13", {"start": v(-5.75, -0.25) * mm, "end": v(-5.75, -9.75) * mm});
            skLineSegment(sketch, "E23.19.0.14", {"start": v(-5.5, -0.25) * mm, "end": v(-5.75, -0.25) * mm});
            skLineSegment(sketch, "E23.19.0.15", {"start": v(-5.5, -9.75) * mm, "end": v(-5.5, -0.25) * mm});
            skLineSegment(sketch, "E23.19.0.16", {"start": v(-5.75, -9.75) * mm, "end": v(-5.5, -9.75) * mm});
            skLineSegment(sketch, "E23.19.0.17", {"start": v(-6, -4) * mm, "end": v(-6, -10) * mm});
            skLineSegment(sketch, "E23.19.0.18", {"start": v(-6.25, -10) * mm, "end": v(-6.25, -4) * mm});
            skLineSegment(sketch, "E23.19.0.19", {"start": v(-6.25, -4) * mm, "end": v(-6, -4) * mm});
            skLineSegment(sketch, "E23.20.0.0", {"start": v(-5.25, 10) * mm, "end": v(-5.25, 4) * mm});
            skLineSegment(sketch, "E23.20.0.1", {"start": v(-5, 4) * mm, "end": v(-5, 10) * mm});
            skLineSegment(sketch, "E23.20.0.2", {"start": v(-4.75, 0.25) * mm, "end": v(-4.75, 9.75) * mm});
            skLineSegment(sketch, "E23.20.0.3", {"start": v(-4.5, 9.75) * mm, "end": v(-4.5, 0.25) * mm});
            skLineSegment(sketch, "E23.20.0.4", {"start": v(-4.75, 9.75) * mm, "end": v(-4.5, 9.75) * mm});
            skLineSegment(sketch, "E23.20.0.5", {"start": v(-5.25, 4) * mm, "end": v(-5, 4) * mm});
            skLineSegment(sketch, "E23.20.0.6", {"start": v(-4.5, 0.25) * mm, "end": v(-4.75, 0.25) * mm});
            skLineSegment(sketch, "E23.20.0.7", {"start": v(-5.25, 3.5) * mm, "end": v(-5.25, 0) * mm});
            skLineSegment(sketch, "E23.20.0.8", {"start": v(-5, 3.5) * mm, "end": v(-5.25, 3.5) * mm});
            skLineSegment(sketch, "E23.20.0.9", {"start": v(-5, 0) * mm, "end": v(-5, 3.5) * mm});
            skLineSegment(sketch, "E23.20.0.10", {"start": v(-5.25, -3.5) * mm, "end": v(-5.25, 0) * mm});
            skLineSegment(sketch, "E23.20.0.11", {"start": v(-5, -3.5) * mm, "end": v(-5.25, -3.5) * mm});
            skLineSegment(sketch, "E23.20.0.12", {"start": v(-5, 0) * mm, "end": v(-5, -3.5) * mm});
            skLineSegment(sketch, "E23.20.0.13", {"start": v(-4.75, -0.25) * mm, "end": v(-4.75, -9.75) * mm});
            skLineSegment(sketch, "E23.20.0.14", {"start": v(-4.5, -0.25) * mm, "end": v(-4.75, -0.25) * mm});
            skLineSegment(sketch, "E23.20.0.15", {"start": v(-4.5, -9.75) * mm, "end": v(-4.5, -0.25) * mm});
            skLineSegment(sketch, "E23.20.0.16", {"start": v(-4.75, -9.75) * mm, "end": v(-4.5, -9.75) * mm});
            skLineSegment(sketch, "E23.20.0.17", {"start": v(-5, -4) * mm, "end": v(-5, -10) * mm});
            skLineSegment(sketch, "E23.20.0.18", {"start": v(-5.25, -10) * mm, "end": v(-5.25, -4) * mm});
            skLineSegment(sketch, "E23.20.0.19", {"start": v(-5.25, -4) * mm, "end": v(-5, -4) * mm});
            skLineSegment(sketch, "E23.21.0.0", {"start": v(-4.25, 10) * mm, "end": v(-4.25, 4) * mm});
            skLineSegment(sketch, "E23.21.0.1", {"start": v(-4, 4) * mm, "end": v(-4, 10) * mm});
            skLineSegment(sketch, "E23.21.0.2", {"start": v(-3.75, 0.25) * mm, "end": v(-3.75, 9.75) * mm});
            skLineSegment(sketch, "E23.21.0.3", {"start": v(-3.5, 9.75) * mm, "end": v(-3.5, 0.25) * mm});
            skLineSegment(sketch, "E23.21.0.4", {"start": v(-3.75, 9.75) * mm, "end": v(-3.5, 9.75) * mm});
            skLineSegment(sketch, "E23.21.0.5", {"start": v(-4.25, 4) * mm, "end": v(-4, 4) * mm});
            skLineSegment(sketch, "E23.21.0.6", {"start": v(-3.5, 0.25) * mm, "end": v(-3.75, 0.25) * mm});
            skLineSegment(sketch, "E23.21.0.7", {"start": v(-4.25, 3.5) * mm, "end": v(-4.25, 0) * mm});
            skLineSegment(sketch, "E23.21.0.8", {"start": v(-4, 3.5) * mm, "end": v(-4.25, 3.5) * mm});
            skLineSegment(sketch, "E23.21.0.9", {"start": v(-4, 0) * mm, "end": v(-4, 3.5) * mm});
            skLineSegment(sketch, "E23.21.0.10", {"start": v(-4.25, -3.5) * mm, "end": v(-4.25, 0) * mm});
            skLineSegment(sketch, "E23.21.0.11", {"start": v(-4, -3.5) * mm, "end": v(-4.25, -3.5) * mm});
            skLineSegment(sketch, "E23.21.0.12", {"start": v(-4, 0) * mm, "end": v(-4, -3.5) * mm});
            skLineSegment(sketch, "E23.21.0.13", {"start": v(-3.75, -0.25) * mm, "end": v(-3.75, -9.75) * mm});
            skLineSegment(sketch, "E23.21.0.14", {"start": v(-3.5, -0.25) * mm, "end": v(-3.75, -0.25) * mm});
            skLineSegment(sketch, "E23.21.0.15", {"start": v(-3.5, -9.75) * mm, "end": v(-3.5, -0.25) * mm});
            skLineSegment(sketch, "E23.21.0.16", {"start": v(-3.75, -9.75) * mm, "end": v(-3.5, -9.75) * mm});
            skLineSegment(sketch, "E23.21.0.17", {"start": v(-4, -4) * mm, "end": v(-4, -10) * mm});
            skLineSegment(sketch, "E23.21.0.18", {"start": v(-4.25, -10) * mm, "end": v(-4.25, -4) * mm});
            skLineSegment(sketch, "E23.21.0.19", {"start": v(-4.25, -4) * mm, "end": v(-4, -4) * mm});
            skLineSegment(sketch, "E23.22.0.0", {"start": v(-3.25, 10) * mm, "end": v(-3.25, 4) * mm});
            skLineSegment(sketch, "E23.22.0.1", {"start": v(-3, 4) * mm, "end": v(-3, 10) * mm});
            skLineSegment(sketch, "E23.22.0.2", {"start": v(-2.75, 0.25) * mm, "end": v(-2.75, 9.75) * mm});
            skLineSegment(sketch, "E23.22.0.3", {"start": v(-2.5, 9.75) * mm, "end": v(-2.5, 0.25) * mm});
            skLineSegment(sketch, "E23.22.0.4", {"start": v(-2.75, 9.75) * mm, "end": v(-2.5, 9.75) * mm});
            skLineSegment(sketch, "E23.22.0.5", {"start": v(-3.25, 4) * mm, "end": v(-3, 4) * mm});
            skLineSegment(sketch, "E23.22.0.6", {"start": v(-2.5, 0.25) * mm, "end": v(-2.75, 0.25) * mm});
            skLineSegment(sketch, "E23.22.0.7", {"start": v(-3.25, 3.5) * mm, "end": v(-3.25, 0) * mm});
            skLineSegment(sketch, "E23.22.0.8", {"start": v(-3, 3.5) * mm, "end": v(-3.25, 3.5) * mm});
            skLineSegment(sketch, "E23.22.0.9", {"start": v(-3, 0) * mm, "end": v(-3, 3.5) * mm});
            skLineSegment(sketch, "E23.22.0.10", {"start": v(-3.25, -3.5) * mm, "end": v(-3.25, 0) * mm});
            skLineSegment(sketch, "E23.22.0.11", {"start": v(-3, -3.5) * mm, "end": v(-3.25, -3.5) * mm});
            skLineSegment(sketch, "E23.22.0.12", {"start": v(-3, 0) * mm, "end": v(-3, -3.5) * mm});
            skLineSegment(sketch, "E23.22.0.13", {"start": v(-2.75, -0.25) * mm, "end": v(-2.75, -9.75) * mm});
            skLineSegment(sketch, "E23.22.0.14", {"start": v(-2.5, -0.25) * mm, "end": v(-2.75, -0.25) * mm});
            skLineSegment(sketch, "E23.22.0.15", {"start": v(-2.5, -9.75) * mm, "end": v(-2.5, -0.25) * mm});
            skLineSegment(sketch, "E23.22.0.16", {"start": v(-2.75, -9.75) * mm, "end": v(-2.5, -9.75) * mm});
            skLineSegment(sketch, "E23.22.0.17", {"start": v(-3, -4) * mm, "end": v(-3, -10) * mm});
            skLineSegment(sketch, "E23.22.0.18", {"start": v(-3.25, -10) * mm, "end": v(-3.25, -4) * mm});
            skLineSegment(sketch, "E23.22.0.19", {"start": v(-3.25, -4) * mm, "end": v(-3, -4) * mm});
            skLineSegment(sketch, "E23.23.0.0", {"start": v(-2.25, 10) * mm, "end": v(-2.25, 4) * mm});
            skLineSegment(sketch, "E23.23.0.1", {"start": v(-2, 4) * mm, "end": v(-2, 10) * mm});
            skLineSegment(sketch, "E23.23.0.2", {"start": v(-1.75, 0.25) * mm, "end": v(-1.75, 9.75) * mm});
            skLineSegment(sketch, "E23.23.0.3", {"start": v(-1.5, 9.75) * mm, "end": v(-1.5, 0.25) * mm});
            skLineSegment(sketch, "E23.23.0.4", {"start": v(-1.75, 9.75) * mm, "end": v(-1.5, 9.75) * mm});
            skLineSegment(sketch, "E23.23.0.5", {"start": v(-2.25, 4) * mm, "end": v(-2, 4) * mm});
            skLineSegment(sketch, "E23.23.0.6", {"start": v(-1.5, 0.25) * mm, "end": v(-1.75, 0.25) * mm});
            skLineSegment(sketch, "E23.23.0.7", {"start": v(-2.25, 3.5) * mm, "end": v(-2.25, 0) * mm});
            skLineSegment(sketch, "E23.23.0.8", {"start": v(-2, 3.5) * mm, "end": v(-2.25, 3.5) * mm});
            skLineSegment(sketch, "E23.23.0.9", {"start": v(-2, 0) * mm, "end": v(-2, 3.5) * mm});
            skLineSegment(sketch, "E23.23.0.10", {"start": v(-2.25, -3.5) * mm, "end": v(-2.25, 0) * mm});
            skLineSegment(sketch, "E23.23.0.11", {"start": v(-2, -3.5) * mm, "end": v(-2.25, -3.5) * mm});
            skLineSegment(sketch, "E23.23.0.12", {"start": v(-2, 0) * mm, "end": v(-2, -3.5) * mm});
            skLineSegment(sketch, "E23.23.0.13", {"start": v(-1.75, -0.25) * mm, "end": v(-1.75, -9.75) * mm});
            skLineSegment(sketch, "E23.23.0.14", {"start": v(-1.5, -0.25) * mm, "end": v(-1.75, -0.25) * mm});
            skLineSegment(sketch, "E23.23.0.15", {"start": v(-1.5, -9.75) * mm, "end": v(-1.5, -0.25) * mm});
            skLineSegment(sketch, "E23.23.0.16", {"start": v(-1.75, -9.75) * mm, "end": v(-1.5, -9.75) * mm});
            skLineSegment(sketch, "E23.23.0.17", {"start": v(-2, -4) * mm, "end": v(-2, -10) * mm});
            skLineSegment(sketch, "E23.23.0.18", {"start": v(-2.25, -10) * mm, "end": v(-2.25, -4) * mm});
            skLineSegment(sketch, "E23.23.0.19", {"start": v(-2.25, -4) * mm, "end": v(-2, -4) * mm});
            skLineSegment(sketch, "E23.24.0.0", {"start": v(-1.25, 10) * mm, "end": v(-1.25, 4) * mm});
            skLineSegment(sketch, "E23.24.0.1", {"start": v(-1, 4) * mm, "end": v(-1, 10) * mm});
            skLineSegment(sketch, "E23.24.0.2", {"start": v(-0.75, 0.25) * mm, "end": v(-0.75, 9.75) * mm});
            skLineSegment(sketch, "E23.24.0.3", {"start": v(-0.5, 9.75) * mm, "end": v(-0.5, 0.25) * mm});
            skLineSegment(sketch, "E23.24.0.4", {"start": v(-0.75, 9.75) * mm, "end": v(-0.5, 9.75) * mm});
            skLineSegment(sketch, "E23.24.0.5", {"start": v(-1.25, 4) * mm, "end": v(-1, 4) * mm});
            skLineSegment(sketch, "E23.24.0.6", {"start": v(-0.5, 0.25) * mm, "end": v(-0.75, 0.25) * mm});
            skLineSegment(sketch, "E23.24.0.7", {"start": v(-1.25, 3.5) * mm, "end": v(-1.25, 0) * mm});
            skLineSegment(sketch, "E23.24.0.8", {"start": v(-1, 3.5) * mm, "end": v(-1.25, 3.5) * mm});
            skLineSegment(sketch, "E23.24.0.9", {"start": v(-1, 0) * mm, "end": v(-1, 3.5) * mm});
            skLineSegment(sketch, "E23.24.0.10", {"start": v(-1.25, -3.5) * mm, "end": v(-1.25, 0) * mm});
            skLineSegment(sketch, "E23.24.0.11", {"start": v(-1, -3.5) * mm, "end": v(-1.25, -3.5) * mm});
            skLineSegment(sketch, "E23.24.0.12", {"start": v(-1, 0) * mm, "end": v(-1, -3.5) * mm});
            skLineSegment(sketch, "E23.24.0.13", {"start": v(-0.75, -0.25) * mm, "end": v(-0.75, -9.75) * mm});
            skLineSegment(sketch, "E23.24.0.14", {"start": v(-0.5, -0.25) * mm, "end": v(-0.75, -0.25) * mm});
            skLineSegment(sketch, "E23.24.0.15", {"start": v(-0.5, -9.75) * mm, "end": v(-0.5, -0.25) * mm});
            skLineSegment(sketch, "E23.24.0.16", {"start": v(-0.75, -9.75) * mm, "end": v(-0.5, -9.75) * mm});
            skLineSegment(sketch, "E23.24.0.17", {"start": v(-1, -4) * mm, "end": v(-1, -10) * mm});
            skLineSegment(sketch, "E23.24.0.18", {"start": v(-1.25, -10) * mm, "end": v(-1.25, -4) * mm});
            skLineSegment(sketch, "E23.24.0.19", {"start": v(-1.25, -4) * mm, "end": v(-1, -4) * mm});
            skLineSegment(sketch, "E23.direction1", {"start": v(-25.25, 4) * mm, "end": v(-24.25, 4) * mm, "construction": true});
            skLineSegment(sketch, "E24.0.25.0", {"start": v(-0.25, 10) * mm, "end": v(-0.25, 4) * mm});
            skLineSegment(sketch, "E24.3.25.0", {"start": v(0, 4) * mm, "end": v(0, 10) * mm});
            skLineSegment(sketch, "E24.6.25.0", {"start": v(0.25, 0.25) * mm, "end": v(0.25, 9.75) * mm});
            skLineSegment(sketch, "E24.9.25.0", {"start": v(0.5, 9.75) * mm, "end": v(0.5, 0.25) * mm});
            skLineSegment(sketch, "E24.12.25.0", {"start": v(0.25, 9.75) * mm, "end": v(0.5, 9.75) * mm});
            skLineSegment(sketch, "E24.15.25.0", {"start": v(-0.25, 4) * mm, "end": v(0, 4) * mm});
            skLineSegment(sketch, "E24.18.25.0", {"start": v(0.5, 0.25) * mm, "end": v(0.25, 0.25) * mm});
            skLineSegment(sketch, "E24.21.25.0", {"start": v(-0.25, 3.5) * mm, "end": v(-0.25, 0) * mm});
            skLineSegment(sketch, "E24.24.25.0", {"start": v(0, 3.5) * mm, "end": v(-0.25, 3.5) * mm});
            skLineSegment(sketch, "E24.27.25.0", {"start": v(0, 0) * mm, "end": v(0, 3.5) * mm});
            skLineSegment(sketch, "E24.30.25.0", {"start": v(-0.25, -3.5) * mm, "end": v(-0.25, 0) * mm});
            skLineSegment(sketch, "E24.33.25.0", {"start": v(0, -3.5) * mm, "end": v(-0.25, -3.5) * mm});
            skLineSegment(sketch, "E24.36.25.0", {"start": v(0, 0) * mm, "end": v(0, -3.5) * mm});
            skLineSegment(sketch, "E24.39.25.0", {"start": v(0.25, -0.25) * mm, "end": v(0.25, -9.75) * mm});
            skLineSegment(sketch, "E24.42.25.0", {"start": v(0.5, -0.25) * mm, "end": v(0.25, -0.25) * mm});
            skLineSegment(sketch, "E24.45.25.0", {"start": v(0.5, -9.75) * mm, "end": v(0.5, -0.25) * mm});
            skLineSegment(sketch, "E24.48.25.0", {"start": v(0.25, -9.75) * mm, "end": v(0.5, -9.75) * mm});
            skLineSegment(sketch, "E24.51.25.0", {"start": v(0, -4) * mm, "end": v(0, -10) * mm});
            skLineSegment(sketch, "E24.54.25.0", {"start": v(-0.25, -10) * mm, "end": v(-0.25, -4) * mm});
            skLineSegment(sketch, "E24.57.25.0", {"start": v(-0.25, -4) * mm, "end": v(0, -4) * mm});
            skLineSegment(sketch, "E25.trimOffspring", {"start": v(-24.25, 10) * mm, "end": v(-25, 10) * mm});
            skLineSegment(sketch, "E26.0.26.0", {"start": v(0.75, 10) * mm, "end": v(0.75, 4) * mm});
            skLineSegment(sketch, "E26.3.26.0", {"start": v(1, 4) * mm, "end": v(1, 10) * mm});
            skLineSegment(sketch, "E26.6.26.0", {"start": v(1.25, 0.25) * mm, "end": v(1.25, 9.75) * mm});
            skLineSegment(sketch, "E26.9.26.0", {"start": v(1.5, 9.75) * mm, "end": v(1.5, 0.25) * mm});
            skLineSegment(sketch, "E26.12.26.0", {"start": v(1.25, 9.75) * mm, "end": v(1.5, 9.75) * mm});
            skLineSegment(sketch, "E26.15.26.0", {"start": v(0.75, 4) * mm, "end": v(1, 4) * mm});
            skLineSegment(sketch, "E26.18.26.0", {"start": v(1.5, 0.25) * mm, "end": v(1.25, 0.25) * mm});
            skLineSegment(sketch, "E26.21.26.0", {"start": v(0.75, 3.5) * mm, "end": v(0.75, 0) * mm});
            skLineSegment(sketch, "E26.24.26.0", {"start": v(1, 3.5) * mm, "end": v(0.75, 3.5) * mm});
            skLineSegment(sketch, "E26.27.26.0", {"start": v(1, 0) * mm, "end": v(1, 3.5) * mm});
            skLineSegment(sketch, "E26.30.26.0", {"start": v(0.75, -3.5) * mm, "end": v(0.75, 0) * mm});
            skLineSegment(sketch, "E26.33.26.0", {"start": v(1, -3.5) * mm, "end": v(0.75, -3.5) * mm});
            skLineSegment(sketch, "E26.36.26.0", {"start": v(1, 0) * mm, "end": v(1, -3.5) * mm});
            skLineSegment(sketch, "E26.39.26.0", {"start": v(1.25, -0.25) * mm, "end": v(1.25, -9.75) * mm});
            skLineSegment(sketch, "E26.42.26.0", {"start": v(1.5, -0.25) * mm, "end": v(1.25, -0.25) * mm});
            skLineSegment(sketch, "E26.45.26.0", {"start": v(1.5, -9.75) * mm, "end": v(1.5, -0.25) * mm});
            skLineSegment(sketch, "E26.48.26.0", {"start": v(1.25, -9.75) * mm, "end": v(1.5, -9.75) * mm});
            skLineSegment(sketch, "E26.51.26.0", {"start": v(1, -4) * mm, "end": v(1, -10) * mm});
            skLineSegment(sketch, "E26.54.26.0", {"start": v(0.75, -10) * mm, "end": v(0.75, -4) * mm});
            skLineSegment(sketch, "E26.57.26.0", {"start": v(0.75, -4) * mm, "end": v(1, -4) * mm});
            skLineSegment(sketch, "E26.0.27.0", {"start": v(1.75, 10) * mm, "end": v(1.75, 4) * mm});
            skLineSegment(sketch, "E26.3.27.0", {"start": v(2, 4) * mm, "end": v(2, 10) * mm});
            skLineSegment(sketch, "E26.6.27.0", {"start": v(2.25, 0.25) * mm, "end": v(2.25, 9.75) * mm});
            skLineSegment(sketch, "E26.9.27.0", {"start": v(2.5, 9.75) * mm, "end": v(2.5, 0.25) * mm});
            skLineSegment(sketch, "E26.12.27.0", {"start": v(2.25, 9.75) * mm, "end": v(2.5, 9.75) * mm});
            skLineSegment(sketch, "E26.15.27.0", {"start": v(1.75, 4) * mm, "end": v(2, 4) * mm});
            skLineSegment(sketch, "E26.18.27.0", {"start": v(2.5, 0.25) * mm, "end": v(2.25, 0.25) * mm});
            skLineSegment(sketch, "E26.21.27.0", {"start": v(1.75, 3.5) * mm, "end": v(1.75, 0) * mm});
            skLineSegment(sketch, "E26.24.27.0", {"start": v(2, 3.5) * mm, "end": v(1.75, 3.5) * mm});
            skLineSegment(sketch, "E26.27.27.0", {"start": v(2, 0) * mm, "end": v(2, 3.5) * mm});
            skLineSegment(sketch, "E26.30.27.0", {"start": v(1.75, -3.5) * mm, "end": v(1.75, 0) * mm});
            skLineSegment(sketch, "E26.33.27.0", {"start": v(2, -3.5) * mm, "end": v(1.75, -3.5) * mm});
            skLineSegment(sketch, "E26.36.27.0", {"start": v(2, 0) * mm, "end": v(2, -3.5) * mm});
            skLineSegment(sketch, "E26.39.27.0", {"start": v(2.25, -0.25) * mm, "end": v(2.25, -9.75) * mm});
            skLineSegment(sketch, "E26.42.27.0", {"start": v(2.5, -0.25) * mm, "end": v(2.25, -0.25) * mm});
            skLineSegment(sketch, "E26.45.27.0", {"start": v(2.5, -9.75) * mm, "end": v(2.5, -0.25) * mm});
            skLineSegment(sketch, "E26.48.27.0", {"start": v(2.25, -9.75) * mm, "end": v(2.5, -9.75) * mm});
            skLineSegment(sketch, "E26.51.27.0", {"start": v(2, -4) * mm, "end": v(2, -10) * mm});
            skLineSegment(sketch, "E26.54.27.0", {"start": v(1.75, -10) * mm, "end": v(1.75, -4) * mm});
            skLineSegment(sketch, "E26.57.27.0", {"start": v(1.75, -4) * mm, "end": v(2, -4) * mm});
            skLineSegment(sketch, "E26.0.28.0", {"start": v(2.75, 10) * mm, "end": v(2.75, 4) * mm});
            skLineSegment(sketch, "E26.3.28.0", {"start": v(3, 4) * mm, "end": v(3, 10) * mm});
            skLineSegment(sketch, "E26.6.28.0", {"start": v(3.25, 0.25) * mm, "end": v(3.25, 9.75) * mm});
            skLineSegment(sketch, "E26.9.28.0", {"start": v(3.5, 9.75) * mm, "end": v(3.5, 0.25) * mm});
            skLineSegment(sketch, "E26.12.28.0", {"start": v(3.25, 9.75) * mm, "end": v(3.5, 9.75) * mm});
            skLineSegment(sketch, "E26.15.28.0", {"start": v(2.75, 4) * mm, "end": v(3, 4) * mm});
            skLineSegment(sketch, "E26.18.28.0", {"start": v(3.5, 0.25) * mm, "end": v(3.25, 0.25) * mm});
            skLineSegment(sketch, "E26.21.28.0", {"start": v(2.75, 3.5) * mm, "end": v(2.75, 0) * mm});
            skLineSegment(sketch, "E26.24.28.0", {"start": v(3, 3.5) * mm, "end": v(2.75, 3.5) * mm});
            skLineSegment(sketch, "E26.27.28.0", {"start": v(3, 0) * mm, "end": v(3, 3.5) * mm});
            skLineSegment(sketch, "E26.30.28.0", {"start": v(2.75, -3.5) * mm, "end": v(2.75, 0) * mm});
            skLineSegment(sketch, "E26.33.28.0", {"start": v(3, -3.5) * mm, "end": v(2.75, -3.5) * mm});
            skLineSegment(sketch, "E26.36.28.0", {"start": v(3, 0) * mm, "end": v(3, -3.5) * mm});
            skLineSegment(sketch, "E26.39.28.0", {"start": v(3.25, -0.25) * mm, "end": v(3.25, -9.75) * mm});
            skLineSegment(sketch, "E26.42.28.0", {"start": v(3.5, -0.25) * mm, "end": v(3.25, -0.25) * mm});
            skLineSegment(sketch, "E26.45.28.0", {"start": v(3.5, -9.75) * mm, "end": v(3.5, -0.25) * mm});
            skLineSegment(sketch, "E26.48.28.0", {"start": v(3.25, -9.75) * mm, "end": v(3.5, -9.75) * mm});
            skLineSegment(sketch, "E26.51.28.0", {"start": v(3, -4) * mm, "end": v(3, -10) * mm});
            skLineSegment(sketch, "E26.54.28.0", {"start": v(2.75, -10) * mm, "end": v(2.75, -4) * mm});
            skLineSegment(sketch, "E26.57.28.0", {"start": v(2.75, -4) * mm, "end": v(3, -4) * mm});
            skLineSegment(sketch, "E26.0.29.0", {"start": v(3.75, 10) * mm, "end": v(3.75, 4) * mm});
            skLineSegment(sketch, "E26.3.29.0", {"start": v(4, 4) * mm, "end": v(4, 10) * mm});
            skLineSegment(sketch, "E26.6.29.0", {"start": v(4.25, 0.25) * mm, "end": v(4.25, 9.75) * mm});
            skLineSegment(sketch, "E26.9.29.0", {"start": v(4.5, 9.75) * mm, "end": v(4.5, 0.25) * mm});
            skLineSegment(sketch, "E26.12.29.0", {"start": v(4.25, 9.75) * mm, "end": v(4.5, 9.75) * mm});
            skLineSegment(sketch, "E26.15.29.0", {"start": v(3.75, 4) * mm, "end": v(4, 4) * mm});
            skLineSegment(sketch, "E26.18.29.0", {"start": v(4.5, 0.25) * mm, "end": v(4.25, 0.25) * mm});
            skLineSegment(sketch, "E26.21.29.0", {"start": v(3.75, 3.5) * mm, "end": v(3.75, 0) * mm});
            skLineSegment(sketch, "E26.24.29.0", {"start": v(4, 3.5) * mm, "end": v(3.75, 3.5) * mm});
            skLineSegment(sketch, "E26.27.29.0", {"start": v(4, 0) * mm, "end": v(4, 3.5) * mm});
            skLineSegment(sketch, "E26.30.29.0", {"start": v(3.75, -3.5) * mm, "end": v(3.75, 0) * mm});
            skLineSegment(sketch, "E26.33.29.0", {"start": v(4, -3.5) * mm, "end": v(3.75, -3.5) * mm});
            skLineSegment(sketch, "E26.36.29.0", {"start": v(4, 0) * mm, "end": v(4, -3.5) * mm});
            skLineSegment(sketch, "E26.39.29.0", {"start": v(4.25, -0.25) * mm, "end": v(4.25, -9.75) * mm});
            skLineSegment(sketch, "E26.42.29.0", {"start": v(4.5, -0.25) * mm, "end": v(4.25, -0.25) * mm});
            skLineSegment(sketch, "E26.45.29.0", {"start": v(4.5, -9.75) * mm, "end": v(4.5, -0.25) * mm});
            skLineSegment(sketch, "E26.48.29.0", {"start": v(4.25, -9.75) * mm, "end": v(4.5, -9.75) * mm});
            skLineSegment(sketch, "E26.51.29.0", {"start": v(4, -4) * mm, "end": v(4, -10) * mm});
            skLineSegment(sketch, "E26.54.29.0", {"start": v(3.75, -10) * mm, "end": v(3.75, -4) * mm});
            skLineSegment(sketch, "E26.57.29.0", {"start": v(3.75, -4) * mm, "end": v(4, -4) * mm});
            skLineSegment(sketch, "E26.0.30.0", {"start": v(4.75, 10) * mm, "end": v(4.75, 4) * mm});
            skLineSegment(sketch, "E26.3.30.0", {"start": v(5, 4) * mm, "end": v(5, 10) * mm});
            skLineSegment(sketch, "E26.6.30.0", {"start": v(5.25, 0.25) * mm, "end": v(5.25, 9.75) * mm});
            skLineSegment(sketch, "E26.9.30.0", {"start": v(5.5, 9.75) * mm, "end": v(5.5, 0.25) * mm});
            skLineSegment(sketch, "E26.12.30.0", {"start": v(5.25, 9.75) * mm, "end": v(5.5, 9.75) * mm});
            skLineSegment(sketch, "E26.15.30.0", {"start": v(4.75, 4) * mm, "end": v(5, 4) * mm});
            skLineSegment(sketch, "E26.18.30.0", {"start": v(5.5, 0.25) * mm, "end": v(5.25, 0.25) * mm});
            skLineSegment(sketch, "E26.21.30.0", {"start": v(4.75, 3.5) * mm, "end": v(4.75, 0) * mm});
            skLineSegment(sketch, "E26.24.30.0", {"start": v(5, 3.5) * mm, "end": v(4.75, 3.5) * mm});
            skLineSegment(sketch, "E26.27.30.0", {"start": v(5, 0) * mm, "end": v(5, 3.5) * mm});
            skLineSegment(sketch, "E26.30.30.0", {"start": v(4.75, -3.5) * mm, "end": v(4.75, 0) * mm});
            skLineSegment(sketch, "E26.33.30.0", {"start": v(5, -3.5) * mm, "end": v(4.75, -3.5) * mm});
            skLineSegment(sketch, "E26.36.30.0", {"start": v(5, 0) * mm, "end": v(5, -3.5) * mm});
            skLineSegment(sketch, "E26.39.30.0", {"start": v(5.25, -0.25) * mm, "end": v(5.25, -9.75) * mm});
            skLineSegment(sketch, "E26.42.30.0", {"start": v(5.5, -0.25) * mm, "end": v(5.25, -0.25) * mm});
            skLineSegment(sketch, "E26.45.30.0", {"start": v(5.5, -9.75) * mm, "end": v(5.5, -0.25) * mm});
            skLineSegment(sketch, "E26.48.30.0", {"start": v(5.25, -9.75) * mm, "end": v(5.5, -9.75) * mm});
            skLineSegment(sketch, "E26.51.30.0", {"start": v(5, -4) * mm, "end": v(5, -10) * mm});
            skLineSegment(sketch, "E26.54.30.0", {"start": v(4.75, -10) * mm, "end": v(4.75, -4) * mm});
            skLineSegment(sketch, "E26.57.30.0", {"start": v(4.75, -4) * mm, "end": v(5, -4) * mm});
            skLineSegment(sketch, "E26.0.31.0", {"start": v(5.75, 10) * mm, "end": v(5.75, 4) * mm});
            skLineSegment(sketch, "E26.3.31.0", {"start": v(6, 4) * mm, "end": v(6, 10) * mm});
            skLineSegment(sketch, "E26.6.31.0", {"start": v(6.25, 0.25) * mm, "end": v(6.25, 9.75) * mm});
            skLineSegment(sketch, "E26.9.31.0", {"start": v(6.5, 9.75) * mm, "end": v(6.5, 0.25) * mm});
            skLineSegment(sketch, "E26.12.31.0", {"start": v(6.25, 9.75) * mm, "end": v(6.5, 9.75) * mm});
            skLineSegment(sketch, "E26.15.31.0", {"start": v(5.75, 4) * mm, "end": v(6, 4) * mm});
            skLineSegment(sketch, "E26.18.31.0", {"start": v(6.5, 0.25) * mm, "end": v(6.25, 0.25) * mm});
            skLineSegment(sketch, "E26.21.31.0", {"start": v(5.75, 3.5) * mm, "end": v(5.75, 0) * mm});
            skLineSegment(sketch, "E26.24.31.0", {"start": v(6, 3.5) * mm, "end": v(5.75, 3.5) * mm});
            skLineSegment(sketch, "E26.27.31.0", {"start": v(6, 0) * mm, "end": v(6, 3.5) * mm});
            skLineSegment(sketch, "E26.30.31.0", {"start": v(5.75, -3.5) * mm, "end": v(5.75, 0) * mm});
            skLineSegment(sketch, "E26.33.31.0", {"start": v(6, -3.5) * mm, "end": v(5.75, -3.5) * mm});
            skLineSegment(sketch, "E26.36.31.0", {"start": v(6, 0) * mm, "end": v(6, -3.5) * mm});
            skLineSegment(sketch, "E26.39.31.0", {"start": v(6.25, -0.25) * mm, "end": v(6.25, -9.75) * mm});
            skLineSegment(sketch, "E26.42.31.0", {"start": v(6.5, -0.25) * mm, "end": v(6.25, -0.25) * mm});
            skLineSegment(sketch, "E26.45.31.0", {"start": v(6.5, -9.75) * mm, "end": v(6.5, -0.25) * mm});
            skLineSegment(sketch, "E26.48.31.0", {"start": v(6.25, -9.75) * mm, "end": v(6.5, -9.75) * mm});
            skLineSegment(sketch, "E26.51.31.0", {"start": v(6, -4) * mm, "end": v(6, -10) * mm});
            skLineSegment(sketch, "E26.54.31.0", {"start": v(5.75, -10) * mm, "end": v(5.75, -4) * mm});
            skLineSegment(sketch, "E26.57.31.0", {"start": v(5.75, -4) * mm, "end": v(6, -4) * mm});
            skLineSegment(sketch, "E26.0.32.0", {"start": v(6.75, 10) * mm, "end": v(6.75, 4) * mm});
            skLineSegment(sketch, "E26.3.32.0", {"start": v(7, 4) * mm, "end": v(7, 10) * mm});
            skLineSegment(sketch, "E26.6.32.0", {"start": v(7.25, 0.25) * mm, "end": v(7.25, 9.75) * mm});
            skLineSegment(sketch, "E26.9.32.0", {"start": v(7.5, 9.75) * mm, "end": v(7.5, 0.25) * mm});
            skLineSegment(sketch, "E26.12.32.0", {"start": v(7.25, 9.75) * mm, "end": v(7.5, 9.75) * mm});
            skLineSegment(sketch, "E26.15.32.0", {"start": v(6.75, 4) * mm, "end": v(7, 4) * mm});
            skLineSegment(sketch, "E26.18.32.0", {"start": v(7.5, 0.25) * mm, "end": v(7.25, 0.25) * mm});
            skLineSegment(sketch, "E26.21.32.0", {"start": v(6.75, 3.5) * mm, "end": v(6.75, 0) * mm});
            skLineSegment(sketch, "E26.24.32.0", {"start": v(7, 3.5) * mm, "end": v(6.75, 3.5) * mm});
            skLineSegment(sketch, "E26.27.32.0", {"start": v(7, 0) * mm, "end": v(7, 3.5) * mm});
            skLineSegment(sketch, "E26.30.32.0", {"start": v(6.75, -3.5) * mm, "end": v(6.75, 0) * mm});
            skLineSegment(sketch, "E26.33.32.0", {"start": v(7, -3.5) * mm, "end": v(6.75, -3.5) * mm});
            skLineSegment(sketch, "E26.36.32.0", {"start": v(7, 0) * mm, "end": v(7, -3.5) * mm});
            skLineSegment(sketch, "E26.39.32.0", {"start": v(7.25, -0.25) * mm, "end": v(7.25, -9.75) * mm});
            skLineSegment(sketch, "E26.42.32.0", {"start": v(7.5, -0.25) * mm, "end": v(7.25, -0.25) * mm});
            skLineSegment(sketch, "E26.45.32.0", {"start": v(7.5, -9.75) * mm, "end": v(7.5, -0.25) * mm});
            skLineSegment(sketch, "E26.48.32.0", {"start": v(7.25, -9.75) * mm, "end": v(7.5, -9.75) * mm});
            skLineSegment(sketch, "E26.51.32.0", {"start": v(7, -4) * mm, "end": v(7, -10) * mm});
            skLineSegment(sketch, "E26.54.32.0", {"start": v(6.75, -10) * mm, "end": v(6.75, -4) * mm});
            skLineSegment(sketch, "E26.57.32.0", {"start": v(6.75, -4) * mm, "end": v(7, -4) * mm});
            skLineSegment(sketch, "E26.0.33.0", {"start": v(7.75, 10) * mm, "end": v(7.75, 4) * mm});
            skLineSegment(sketch, "E26.3.33.0", {"start": v(8, 4) * mm, "end": v(8, 10) * mm});
            skLineSegment(sketch, "E26.6.33.0", {"start": v(8.25, 0.25) * mm, "end": v(8.25, 9.75) * mm});
            skLineSegment(sketch, "E26.9.33.0", {"start": v(8.5, 9.75) * mm, "end": v(8.5, 0.25) * mm});
            skLineSegment(sketch, "E26.12.33.0", {"start": v(8.25, 9.75) * mm, "end": v(8.5, 9.75) * mm});
            skLineSegment(sketch, "E26.15.33.0", {"start": v(7.75, 4) * mm, "end": v(8, 4) * mm});
            skLineSegment(sketch, "E26.18.33.0", {"start": v(8.5, 0.25) * mm, "end": v(8.25, 0.25) * mm});
            skLineSegment(sketch, "E26.21.33.0", {"start": v(7.75, 3.5) * mm, "end": v(7.75, 0) * mm});
            skLineSegment(sketch, "E26.24.33.0", {"start": v(8, 3.5) * mm, "end": v(7.75, 3.5) * mm});
            skLineSegment(sketch, "E26.27.33.0", {"start": v(8, 0) * mm, "end": v(8, 3.5) * mm});
            skLineSegment(sketch, "E26.30.33.0", {"start": v(7.75, -3.5) * mm, "end": v(7.75, 0) * mm});
            skLineSegment(sketch, "E26.33.33.0", {"start": v(8, -3.5) * mm, "end": v(7.75, -3.5) * mm});
            skLineSegment(sketch, "E26.36.33.0", {"start": v(8, 0) * mm, "end": v(8, -3.5) * mm});
            skLineSegment(sketch, "E26.39.33.0", {"start": v(8.25, -0.25) * mm, "end": v(8.25, -9.75) * mm});
            skLineSegment(sketch, "E26.42.33.0", {"start": v(8.5, -0.25) * mm, "end": v(8.25, -0.25) * mm});
            skLineSegment(sketch, "E26.45.33.0", {"start": v(8.5, -9.75) * mm, "end": v(8.5, -0.25) * mm});
            skLineSegment(sketch, "E26.48.33.0", {"start": v(8.25, -9.75) * mm, "end": v(8.5, -9.75) * mm});
            skLineSegment(sketch, "E26.51.33.0", {"start": v(8, -4) * mm, "end": v(8, -10) * mm});
            skLineSegment(sketch, "E26.54.33.0", {"start": v(7.75, -10) * mm, "end": v(7.75, -4) * mm});
            skLineSegment(sketch, "E26.57.33.0", {"start": v(7.75, -4) * mm, "end": v(8, -4) * mm});
            skLineSegment(sketch, "E26.0.34.0", {"start": v(8.75, 10) * mm, "end": v(8.75, 4) * mm});
            skLineSegment(sketch, "E26.3.34.0", {"start": v(9, 4) * mm, "end": v(9, 10) * mm});
            skLineSegment(sketch, "E26.6.34.0", {"start": v(9.25, 0.25) * mm, "end": v(9.25, 9.75) * mm});
            skLineSegment(sketch, "E26.9.34.0", {"start": v(9.5, 9.75) * mm, "end": v(9.5, 0.25) * mm});
            skLineSegment(sketch, "E26.12.34.0", {"start": v(9.25, 9.75) * mm, "end": v(9.5, 9.75) * mm});
            skLineSegment(sketch, "E26.15.34.0", {"start": v(8.75, 4) * mm, "end": v(9, 4) * mm});
            skLineSegment(sketch, "E26.18.34.0", {"start": v(9.5, 0.25) * mm, "end": v(9.25, 0.25) * mm});
            skLineSegment(sketch, "E26.21.34.0", {"start": v(8.75, 3.5) * mm, "end": v(8.75, 0) * mm});
            skLineSegment(sketch, "E26.24.34.0", {"start": v(9, 3.5) * mm, "end": v(8.75, 3.5) * mm});
            skLineSegment(sketch, "E26.27.34.0", {"start": v(9, 0) * mm, "end": v(9, 3.5) * mm});
            skLineSegment(sketch, "E26.30.34.0", {"start": v(8.75, -3.5) * mm, "end": v(8.75, 0) * mm});
            skLineSegment(sketch, "E26.33.34.0", {"start": v(9, -3.5) * mm, "end": v(8.75, -3.5) * mm});
            skLineSegment(sketch, "E26.36.34.0", {"start": v(9, 0) * mm, "end": v(9, -3.5) * mm});
            skLineSegment(sketch, "E26.39.34.0", {"start": v(9.25, -0.25) * mm, "end": v(9.25, -9.75) * mm});
            skLineSegment(sketch, "E26.42.34.0", {"start": v(9.5, -0.25) * mm, "end": v(9.25, -0.25) * mm});
            skLineSegment(sketch, "E26.45.34.0", {"start": v(9.5, -9.75) * mm, "end": v(9.5, -0.25) * mm});
            skLineSegment(sketch, "E26.48.34.0", {"start": v(9.25, -9.75) * mm, "end": v(9.5, -9.75) * mm});
            skLineSegment(sketch, "E26.51.34.0", {"start": v(9, -4) * mm, "end": v(9, -10) * mm});
            skLineSegment(sketch, "E26.54.34.0", {"start": v(8.75, -10) * mm, "end": v(8.75, -4) * mm});
            skLineSegment(sketch, "E26.57.34.0", {"start": v(8.75, -4) * mm, "end": v(9, -4) * mm});
            skLineSegment(sketch, "E26.0.35.0", {"start": v(9.75, 10) * mm, "end": v(9.75, 4) * mm});
            skLineSegment(sketch, "E26.3.35.0", {"start": v(10, 4) * mm, "end": v(10, 10) * mm});
            skLineSegment(sketch, "E26.6.35.0", {"start": v(10.25, 0.25) * mm, "end": v(10.25, 9.75) * mm});
            skLineSegment(sketch, "E26.9.35.0", {"start": v(10.5, 9.75) * mm, "end": v(10.5, 0.25) * mm});
            skLineSegment(sketch, "E26.12.35.0", {"start": v(10.25, 9.75) * mm, "end": v(10.5, 9.75) * mm});
            skLineSegment(sketch, "E26.15.35.0", {"start": v(9.75, 4) * mm, "end": v(10, 4) * mm});
            skLineSegment(sketch, "E26.18.35.0", {"start": v(10.5, 0.25) * mm, "end": v(10.25, 0.25) * mm});
            skLineSegment(sketch, "E26.21.35.0", {"start": v(9.75, 3.5) * mm, "end": v(9.75, 0) * mm});
            skLineSegment(sketch, "E26.24.35.0", {"start": v(10, 3.5) * mm, "end": v(9.75, 3.5) * mm});
            skLineSegment(sketch, "E26.27.35.0", {"start": v(10, 0) * mm, "end": v(10, 3.5) * mm});
            skLineSegment(sketch, "E26.30.35.0", {"start": v(9.75, -3.5) * mm, "end": v(9.75, 0) * mm});
            skLineSegment(sketch, "E26.33.35.0", {"start": v(10, -3.5) * mm, "end": v(9.75, -3.5) * mm});
            skLineSegment(sketch, "E26.36.35.0", {"start": v(10, 0) * mm, "end": v(10, -3.5) * mm});
            skLineSegment(sketch, "E26.39.35.0", {"start": v(10.25, -0.25) * mm, "end": v(10.25, -9.75) * mm});
            skLineSegment(sketch, "E26.42.35.0", {"start": v(10.5, -0.25) * mm, "end": v(10.25, -0.25) * mm});
            skLineSegment(sketch, "E26.45.35.0", {"start": v(10.5, -9.75) * mm, "end": v(10.5, -0.25) * mm});
            skLineSegment(sketch, "E26.48.35.0", {"start": v(10.25, -9.75) * mm, "end": v(10.5, -9.75) * mm});
            skLineSegment(sketch, "E26.51.35.0", {"start": v(10, -4) * mm, "end": v(10, -10) * mm});
            skLineSegment(sketch, "E26.54.35.0", {"start": v(9.75, -10) * mm, "end": v(9.75, -4) * mm});
            skLineSegment(sketch, "E26.57.35.0", {"start": v(9.75, -4) * mm, "end": v(10, -4) * mm});
            skLineSegment(sketch, "E26.0.36.0", {"start": v(10.75, 10) * mm, "end": v(10.75, 4) * mm});
            skLineSegment(sketch, "E26.3.36.0", {"start": v(11, 4) * mm, "end": v(11, 10) * mm});
            skLineSegment(sketch, "E26.6.36.0", {"start": v(11.25, 0.25) * mm, "end": v(11.25, 9.75) * mm});
            skLineSegment(sketch, "E26.9.36.0", {"start": v(11.5, 9.75) * mm, "end": v(11.5, 0.25) * mm});
            skLineSegment(sketch, "E26.12.36.0", {"start": v(11.25, 9.75) * mm, "end": v(11.5, 9.75) * mm});
            skLineSegment(sketch, "E26.15.36.0", {"start": v(10.75, 4) * mm, "end": v(11, 4) * mm});
            skLineSegment(sketch, "E26.18.36.0", {"start": v(11.5, 0.25) * mm, "end": v(11.25, 0.25) * mm});
            skLineSegment(sketch, "E26.21.36.0", {"start": v(10.75, 3.5) * mm, "end": v(10.75, 0) * mm});
            skLineSegment(sketch, "E26.24.36.0", {"start": v(11, 3.5) * mm, "end": v(10.75, 3.5) * mm});
            skLineSegment(sketch, "E26.27.36.0", {"start": v(11, 0) * mm, "end": v(11, 3.5) * mm});
            skLineSegment(sketch, "E26.30.36.0", {"start": v(10.75, -3.5) * mm, "end": v(10.75, 0) * mm});
            skLineSegment(sketch, "E26.33.36.0", {"start": v(11, -3.5) * mm, "end": v(10.75, -3.5) * mm});
            skLineSegment(sketch, "E26.36.36.0", {"start": v(11, 0) * mm, "end": v(11, -3.5) * mm});
            skLineSegment(sketch, "E26.39.36.0", {"start": v(11.25, -0.25) * mm, "end": v(11.25, -9.75) * mm});
            skLineSegment(sketch, "E26.42.36.0", {"start": v(11.5, -0.25) * mm, "end": v(11.25, -0.25) * mm});
            skLineSegment(sketch, "E26.45.36.0", {"start": v(11.5, -9.75) * mm, "end": v(11.5, -0.25) * mm});
            skLineSegment(sketch, "E26.48.36.0", {"start": v(11.25, -9.75) * mm, "end": v(11.5, -9.75) * mm});
            skLineSegment(sketch, "E26.51.36.0", {"start": v(11, -4) * mm, "end": v(11, -10) * mm});
            skLineSegment(sketch, "E26.54.36.0", {"start": v(10.75, -10) * mm, "end": v(10.75, -4) * mm});
            skLineSegment(sketch, "E26.57.36.0", {"start": v(10.75, -4) * mm, "end": v(11, -4) * mm});
            skLineSegment(sketch, "E26.0.37.0", {"start": v(11.75, 10) * mm, "end": v(11.75, 4) * mm});
            skLineSegment(sketch, "E26.3.37.0", {"start": v(12, 4) * mm, "end": v(12, 10) * mm});
            skLineSegment(sketch, "E26.6.37.0", {"start": v(12.25, 0.25) * mm, "end": v(12.25, 9.75) * mm});
            skLineSegment(sketch, "E26.9.37.0", {"start": v(12.5, 9.75) * mm, "end": v(12.5, 0.25) * mm});
            skLineSegment(sketch, "E26.12.37.0", {"start": v(12.25, 9.75) * mm, "end": v(12.5, 9.75) * mm});
            skLineSegment(sketch, "E26.15.37.0", {"start": v(11.75, 4) * mm, "end": v(12, 4) * mm});
            skLineSegment(sketch, "E26.18.37.0", {"start": v(12.5, 0.25) * mm, "end": v(12.25, 0.25) * mm});
            skLineSegment(sketch, "E26.21.37.0", {"start": v(11.75, 3.5) * mm, "end": v(11.75, 0) * mm});
            skLineSegment(sketch, "E26.24.37.0", {"start": v(12, 3.5) * mm, "end": v(11.75, 3.5) * mm});
            skLineSegment(sketch, "E26.27.37.0", {"start": v(12, 0) * mm, "end": v(12, 3.5) * mm});
            skLineSegment(sketch, "E26.30.37.0", {"start": v(11.75, -3.5) * mm, "end": v(11.75, 0) * mm});
            skLineSegment(sketch, "E26.33.37.0", {"start": v(12, -3.5) * mm, "end": v(11.75, -3.5) * mm});
            skLineSegment(sketch, "E26.36.37.0", {"start": v(12, 0) * mm, "end": v(12, -3.5) * mm});
            skLineSegment(sketch, "E26.39.37.0", {"start": v(12.25, -0.25) * mm, "end": v(12.25, -9.75) * mm});
            skLineSegment(sketch, "E26.42.37.0", {"start": v(12.5, -0.25) * mm, "end": v(12.25, -0.25) * mm});
            skLineSegment(sketch, "E26.45.37.0", {"start": v(12.5, -9.75) * mm, "end": v(12.5, -0.25) * mm});
            skLineSegment(sketch, "E26.48.37.0", {"start": v(12.25, -9.75) * mm, "end": v(12.5, -9.75) * mm});
            skLineSegment(sketch, "E26.51.37.0", {"start": v(12, -4) * mm, "end": v(12, -10) * mm});
            skLineSegment(sketch, "E26.54.37.0", {"start": v(11.75, -10) * mm, "end": v(11.75, -4) * mm});
            skLineSegment(sketch, "E26.57.37.0", {"start": v(11.75, -4) * mm, "end": v(12, -4) * mm});
            skLineSegment(sketch, "E26.0.38.0", {"start": v(12.75, 10) * mm, "end": v(12.75, 4) * mm});
            skLineSegment(sketch, "E26.3.38.0", {"start": v(13, 4) * mm, "end": v(13, 10) * mm});
            skLineSegment(sketch, "E26.6.38.0", {"start": v(13.25, 0.25) * mm, "end": v(13.25, 9.75) * mm});
            skLineSegment(sketch, "E26.9.38.0", {"start": v(13.5, 9.75) * mm, "end": v(13.5, 0.25) * mm});
            skLineSegment(sketch, "E26.12.38.0", {"start": v(13.25, 9.75) * mm, "end": v(13.5, 9.75) * mm});
            skLineSegment(sketch, "E26.15.38.0", {"start": v(12.75, 4) * mm, "end": v(13, 4) * mm});
            skLineSegment(sketch, "E26.18.38.0", {"start": v(13.5, 0.25) * mm, "end": v(13.25, 0.25) * mm});
            skLineSegment(sketch, "E26.21.38.0", {"start": v(12.75, 3.5) * mm, "end": v(12.75, 0) * mm});
            skLineSegment(sketch, "E26.24.38.0", {"start": v(13, 3.5) * mm, "end": v(12.75, 3.5) * mm});
            skLineSegment(sketch, "E26.27.38.0", {"start": v(13, 0) * mm, "end": v(13, 3.5) * mm});
            skLineSegment(sketch, "E26.30.38.0", {"start": v(12.75, -3.5) * mm, "end": v(12.75, 0) * mm});
            skLineSegment(sketch, "E26.33.38.0", {"start": v(13, -3.5) * mm, "end": v(12.75, -3.5) * mm});
            skLineSegment(sketch, "E26.36.38.0", {"start": v(13, 0) * mm, "end": v(13, -3.5) * mm});
            skLineSegment(sketch, "E26.39.38.0", {"start": v(13.25, -0.25) * mm, "end": v(13.25, -9.75) * mm});
            skLineSegment(sketch, "E26.42.38.0", {"start": v(13.5, -0.25) * mm, "end": v(13.25, -0.25) * mm});
            skLineSegment(sketch, "E26.45.38.0", {"start": v(13.5, -9.75) * mm, "end": v(13.5, -0.25) * mm});
            skLineSegment(sketch, "E26.48.38.0", {"start": v(13.25, -9.75) * mm, "end": v(13.5, -9.75) * mm});
            skLineSegment(sketch, "E26.51.38.0", {"start": v(13, -4) * mm, "end": v(13, -10) * mm});
            skLineSegment(sketch, "E26.54.38.0", {"start": v(12.75, -10) * mm, "end": v(12.75, -4) * mm});
            skLineSegment(sketch, "E26.57.38.0", {"start": v(12.75, -4) * mm, "end": v(13, -4) * mm});
            skLineSegment(sketch, "E26.0.39.0", {"start": v(13.75, 10) * mm, "end": v(13.75, 4) * mm});
            skLineSegment(sketch, "E26.3.39.0", {"start": v(14, 4) * mm, "end": v(14, 10) * mm});
            skLineSegment(sketch, "E26.6.39.0", {"start": v(14.25, 0.25) * mm, "end": v(14.25, 9.75) * mm});
            skLineSegment(sketch, "E26.9.39.0", {"start": v(14.5, 9.75) * mm, "end": v(14.5, 0.25) * mm});
            skLineSegment(sketch, "E26.12.39.0", {"start": v(14.25, 9.75) * mm, "end": v(14.5, 9.75) * mm});
            skLineSegment(sketch, "E26.15.39.0", {"start": v(13.75, 4) * mm, "end": v(14, 4) * mm});
            skLineSegment(sketch, "E26.18.39.0", {"start": v(14.5, 0.25) * mm, "end": v(14.25, 0.25) * mm});
            skLineSegment(sketch, "E26.21.39.0", {"start": v(13.75, 3.5) * mm, "end": v(13.75, 0) * mm});
            skLineSegment(sketch, "E26.24.39.0", {"start": v(14, 3.5) * mm, "end": v(13.75, 3.5) * mm});
            skLineSegment(sketch, "E26.27.39.0", {"start": v(14, 0) * mm, "end": v(14, 3.5) * mm});
            skLineSegment(sketch, "E26.30.39.0", {"start": v(13.75, -3.5) * mm, "end": v(13.75, 0) * mm});
            skLineSegment(sketch, "E26.33.39.0", {"start": v(14, -3.5) * mm, "end": v(13.75, -3.5) * mm});
            skLineSegment(sketch, "E26.36.39.0", {"start": v(14, 0) * mm, "end": v(14, -3.5) * mm});
            skLineSegment(sketch, "E26.39.39.0", {"start": v(14.25, -0.25) * mm, "end": v(14.25, -9.75) * mm});
            skLineSegment(sketch, "E26.42.39.0", {"start": v(14.5, -0.25) * mm, "end": v(14.25, -0.25) * mm});
            skLineSegment(sketch, "E26.45.39.0", {"start": v(14.5, -9.75) * mm, "end": v(14.5, -0.25) * mm});
            skLineSegment(sketch, "E26.48.39.0", {"start": v(14.25, -9.75) * mm, "end": v(14.5, -9.75) * mm});
            skLineSegment(sketch, "E26.51.39.0", {"start": v(14, -4) * mm, "end": v(14, -10) * mm});
            skLineSegment(sketch, "E26.54.39.0", {"start": v(13.75, -10) * mm, "end": v(13.75, -4) * mm});
            skLineSegment(sketch, "E26.57.39.0", {"start": v(13.75, -4) * mm, "end": v(14, -4) * mm});
            skLineSegment(sketch, "E26.0.40.0", {"start": v(14.75, 10) * mm, "end": v(14.75, 4) * mm});
            skLineSegment(sketch, "E26.3.40.0", {"start": v(15, 4) * mm, "end": v(15, 10) * mm});
            skLineSegment(sketch, "E26.6.40.0", {"start": v(15.25, 0.25) * mm, "end": v(15.25, 9.75) * mm});
            skLineSegment(sketch, "E26.9.40.0", {"start": v(15.5, 9.75) * mm, "end": v(15.5, 0.25) * mm});
            skLineSegment(sketch, "E26.12.40.0", {"start": v(15.25, 9.75) * mm, "end": v(15.5, 9.75) * mm});
            skLineSegment(sketch, "E26.15.40.0", {"start": v(14.75, 4) * mm, "end": v(15, 4) * mm});
            skLineSegment(sketch, "E26.18.40.0", {"start": v(15.5, 0.25) * mm, "end": v(15.25, 0.25) * mm});
            skLineSegment(sketch, "E26.21.40.0", {"start": v(14.75, 3.5) * mm, "end": v(14.75, 0) * mm});
            skLineSegment(sketch, "E26.24.40.0", {"start": v(15, 3.5) * mm, "end": v(14.75, 3.5) * mm});
            skLineSegment(sketch, "E26.27.40.0", {"start": v(15, 0) * mm, "end": v(15, 3.5) * mm});
            skLineSegment(sketch, "E26.30.40.0", {"start": v(14.75, -3.5) * mm, "end": v(14.75, 0) * mm});
            skLineSegment(sketch, "E26.33.40.0", {"start": v(15, -3.5) * mm, "end": v(14.75, -3.5) * mm});
            skLineSegment(sketch, "E26.36.40.0", {"start": v(15, 0) * mm, "end": v(15, -3.5) * mm});
            skLineSegment(sketch, "E26.39.40.0", {"start": v(15.25, -0.25) * mm, "end": v(15.25, -9.75) * mm});
            skLineSegment(sketch, "E26.42.40.0", {"start": v(15.5, -0.25) * mm, "end": v(15.25, -0.25) * mm});
            skLineSegment(sketch, "E26.45.40.0", {"start": v(15.5, -9.75) * mm, "end": v(15.5, -0.25) * mm});
            skLineSegment(sketch, "E26.48.40.0", {"start": v(15.25, -9.75) * mm, "end": v(15.5, -9.75) * mm});
            skLineSegment(sketch, "E26.51.40.0", {"start": v(15, -4) * mm, "end": v(15, -10) * mm});
            skLineSegment(sketch, "E26.54.40.0", {"start": v(14.75, -10) * mm, "end": v(14.75, -4) * mm});
            skLineSegment(sketch, "E26.57.40.0", {"start": v(14.75, -4) * mm, "end": v(15, -4) * mm});
            skLineSegment(sketch, "E26.0.41.0", {"start": v(15.75, 10) * mm, "end": v(15.75, 4) * mm});
            skLineSegment(sketch, "E26.3.41.0", {"start": v(16, 4) * mm, "end": v(16, 10) * mm});
            skLineSegment(sketch, "E26.6.41.0", {"start": v(16.25, 0.25) * mm, "end": v(16.25, 9.75) * mm});
            skLineSegment(sketch, "E26.9.41.0", {"start": v(16.5, 9.75) * mm, "end": v(16.5, 0.25) * mm});
            skLineSegment(sketch, "E26.12.41.0", {"start": v(16.25, 9.75) * mm, "end": v(16.5, 9.75) * mm});
            skLineSegment(sketch, "E26.15.41.0", {"start": v(15.75, 4) * mm, "end": v(16, 4) * mm});
            skLineSegment(sketch, "E26.18.41.0", {"start": v(16.5, 0.25) * mm, "end": v(16.25, 0.25) * mm});
            skLineSegment(sketch, "E26.21.41.0", {"start": v(15.75, 3.5) * mm, "end": v(15.75, 0) * mm});
            skLineSegment(sketch, "E26.24.41.0", {"start": v(16, 3.5) * mm, "end": v(15.75, 3.5) * mm});
            skLineSegment(sketch, "E26.27.41.0", {"start": v(16, 0) * mm, "end": v(16, 3.5) * mm});
            skLineSegment(sketch, "E26.30.41.0", {"start": v(15.75, -3.5) * mm, "end": v(15.75, 0) * mm});
            skLineSegment(sketch, "E26.33.41.0", {"start": v(16, -3.5) * mm, "end": v(15.75, -3.5) * mm});
            skLineSegment(sketch, "E26.36.41.0", {"start": v(16, 0) * mm, "end": v(16, -3.5) * mm});
            skLineSegment(sketch, "E26.39.41.0", {"start": v(16.25, -0.25) * mm, "end": v(16.25, -9.75) * mm});
            skLineSegment(sketch, "E26.42.41.0", {"start": v(16.5, -0.25) * mm, "end": v(16.25, -0.25) * mm});
            skLineSegment(sketch, "E26.45.41.0", {"start": v(16.5, -9.75) * mm, "end": v(16.5, -0.25) * mm});
            skLineSegment(sketch, "E26.48.41.0", {"start": v(16.25, -9.75) * mm, "end": v(16.5, -9.75) * mm});
            skLineSegment(sketch, "E26.51.41.0", {"start": v(16, -4) * mm, "end": v(16, -10) * mm});
            skLineSegment(sketch, "E26.54.41.0", {"start": v(15.75, -10) * mm, "end": v(15.75, -4) * mm});
            skLineSegment(sketch, "E26.57.41.0", {"start": v(15.75, -4) * mm, "end": v(16, -4) * mm});
            skLineSegment(sketch, "E26.0.42.0", {"start": v(16.75, 10) * mm, "end": v(16.75, 4) * mm});
            skLineSegment(sketch, "E26.3.42.0", {"start": v(17, 4) * mm, "end": v(17, 10) * mm});
            skLineSegment(sketch, "E26.6.42.0", {"start": v(17.25, 0.25) * mm, "end": v(17.25, 9.75) * mm});
            skLineSegment(sketch, "E26.9.42.0", {"start": v(17.5, 9.75) * mm, "end": v(17.5, 0.25) * mm});
            skLineSegment(sketch, "E26.12.42.0", {"start": v(17.25, 9.75) * mm, "end": v(17.5, 9.75) * mm});
            skLineSegment(sketch, "E26.15.42.0", {"start": v(16.75, 4) * mm, "end": v(17, 4) * mm});
            skLineSegment(sketch, "E26.18.42.0", {"start": v(17.5, 0.25) * mm, "end": v(17.25, 0.25) * mm});
            skLineSegment(sketch, "E26.21.42.0", {"start": v(16.75, 3.5) * mm, "end": v(16.75, 0) * mm});
            skLineSegment(sketch, "E26.24.42.0", {"start": v(17, 3.5) * mm, "end": v(16.75, 3.5) * mm});
            skLineSegment(sketch, "E26.27.42.0", {"start": v(17, 0) * mm, "end": v(17, 3.5) * mm});
            skLineSegment(sketch, "E26.30.42.0", {"start": v(16.75, -3.5) * mm, "end": v(16.75, 0) * mm});
            skLineSegment(sketch, "E26.33.42.0", {"start": v(17, -3.5) * mm, "end": v(16.75, -3.5) * mm});
            skLineSegment(sketch, "E26.36.42.0", {"start": v(17, 0) * mm, "end": v(17, -3.5) * mm});
            skLineSegment(sketch, "E26.39.42.0", {"start": v(17.25, -0.25) * mm, "end": v(17.25, -9.75) * mm});
            skLineSegment(sketch, "E26.42.42.0", {"start": v(17.5, -0.25) * mm, "end": v(17.25, -0.25) * mm});
            skLineSegment(sketch, "E26.45.42.0", {"start": v(17.5, -9.75) * mm, "end": v(17.5, -0.25) * mm});
            skLineSegment(sketch, "E26.48.42.0", {"start": v(17.25, -9.75) * mm, "end": v(17.5, -9.75) * mm});
            skLineSegment(sketch, "E26.51.42.0", {"start": v(17, -4) * mm, "end": v(17, -10) * mm});
            skLineSegment(sketch, "E26.54.42.0", {"start": v(16.75, -10) * mm, "end": v(16.75, -4) * mm});
            skLineSegment(sketch, "E26.57.42.0", {"start": v(16.75, -4) * mm, "end": v(17, -4) * mm});
            skLineSegment(sketch, "E26.0.43.0", {"start": v(17.75, 10) * mm, "end": v(17.75, 4) * mm});
            skLineSegment(sketch, "E26.3.43.0", {"start": v(18, 4) * mm, "end": v(18, 10) * mm});
            skLineSegment(sketch, "E26.6.43.0", {"start": v(18.25, 0.25) * mm, "end": v(18.25, 9.75) * mm});
            skLineSegment(sketch, "E26.9.43.0", {"start": v(18.5, 9.75) * mm, "end": v(18.5, 0.25) * mm});
            skLineSegment(sketch, "E26.12.43.0", {"start": v(18.25, 9.75) * mm, "end": v(18.5, 9.75) * mm});
            skLineSegment(sketch, "E26.15.43.0", {"start": v(17.75, 4) * mm, "end": v(18, 4) * mm});
            skLineSegment(sketch, "E26.18.43.0", {"start": v(18.5, 0.25) * mm, "end": v(18.25, 0.25) * mm});
            skLineSegment(sketch, "E26.21.43.0", {"start": v(17.75, 3.5) * mm, "end": v(17.75, 0) * mm});
            skLineSegment(sketch, "E26.24.43.0", {"start": v(18, 3.5) * mm, "end": v(17.75, 3.5) * mm});
            skLineSegment(sketch, "E26.27.43.0", {"start": v(18, 0) * mm, "end": v(18, 3.5) * mm});
            skLineSegment(sketch, "E26.30.43.0", {"start": v(17.75, -3.5) * mm, "end": v(17.75, 0) * mm});
            skLineSegment(sketch, "E26.33.43.0", {"start": v(18, -3.5) * mm, "end": v(17.75, -3.5) * mm});
            skLineSegment(sketch, "E26.36.43.0", {"start": v(18, 0) * mm, "end": v(18, -3.5) * mm});
            skLineSegment(sketch, "E26.39.43.0", {"start": v(18.25, -0.25) * mm, "end": v(18.25, -9.75) * mm});
            skLineSegment(sketch, "E26.42.43.0", {"start": v(18.5, -0.25) * mm, "end": v(18.25, -0.25) * mm});
            skLineSegment(sketch, "E26.45.43.0", {"start": v(18.5, -9.75) * mm, "end": v(18.5, -0.25) * mm});
            skLineSegment(sketch, "E26.48.43.0", {"start": v(18.25, -9.75) * mm, "end": v(18.5, -9.75) * mm});
            skLineSegment(sketch, "E26.51.43.0", {"start": v(18, -4) * mm, "end": v(18, -10) * mm});
            skLineSegment(sketch, "E26.54.43.0", {"start": v(17.75, -10) * mm, "end": v(17.75, -4) * mm});
            skLineSegment(sketch, "E26.57.43.0", {"start": v(17.75, -4) * mm, "end": v(18, -4) * mm});
            skLineSegment(sketch, "E26.0.44.0", {"start": v(18.75, 10) * mm, "end": v(18.75, 4) * mm});
            skLineSegment(sketch, "E26.3.44.0", {"start": v(19, 4) * mm, "end": v(19, 10) * mm});
            skLineSegment(sketch, "E26.6.44.0", {"start": v(19.25, 0.25) * mm, "end": v(19.25, 9.75) * mm});
            skLineSegment(sketch, "E26.9.44.0", {"start": v(19.5, 9.75) * mm, "end": v(19.5, 0.25) * mm});
            skLineSegment(sketch, "E26.12.44.0", {"start": v(19.25, 9.75) * mm, "end": v(19.5, 9.75) * mm});
            skLineSegment(sketch, "E26.15.44.0", {"start": v(18.75, 4) * mm, "end": v(19, 4) * mm});
            skLineSegment(sketch, "E26.18.44.0", {"start": v(19.5, 0.25) * mm, "end": v(19.25, 0.25) * mm});
            skLineSegment(sketch, "E26.21.44.0", {"start": v(18.75, 3.5) * mm, "end": v(18.75, 0) * mm});
            skLineSegment(sketch, "E26.24.44.0", {"start": v(19, 3.5) * mm, "end": v(18.75, 3.5) * mm});
            skLineSegment(sketch, "E26.27.44.0", {"start": v(19, 0) * mm, "end": v(19, 3.5) * mm});
            skLineSegment(sketch, "E26.30.44.0", {"start": v(18.75, -3.5) * mm, "end": v(18.75, 0) * mm});
            skLineSegment(sketch, "E26.33.44.0", {"start": v(19, -3.5) * mm, "end": v(18.75, -3.5) * mm});
            skLineSegment(sketch, "E26.36.44.0", {"start": v(19, 0) * mm, "end": v(19, -3.5) * mm});
            skLineSegment(sketch, "E26.39.44.0", {"start": v(19.25, -0.25) * mm, "end": v(19.25, -9.75) * mm});
            skLineSegment(sketch, "E26.42.44.0", {"start": v(19.5, -0.25) * mm, "end": v(19.25, -0.25) * mm});
            skLineSegment(sketch, "E26.45.44.0", {"start": v(19.5, -9.75) * mm, "end": v(19.5, -0.25) * mm});
            skLineSegment(sketch, "E26.48.44.0", {"start": v(19.25, -9.75) * mm, "end": v(19.5, -9.75) * mm});
            skLineSegment(sketch, "E26.51.44.0", {"start": v(19, -4) * mm, "end": v(19, -10) * mm});
            skLineSegment(sketch, "E26.54.44.0", {"start": v(18.75, -10) * mm, "end": v(18.75, -4) * mm});
            skLineSegment(sketch, "E26.57.44.0", {"start": v(18.75, -4) * mm, "end": v(19, -4) * mm});
            skLineSegment(sketch, "E26.0.45.0", {"start": v(19.75, 10) * mm, "end": v(19.75, 4) * mm});
            skLineSegment(sketch, "E26.3.45.0", {"start": v(20, 4) * mm, "end": v(20, 10) * mm});
            skLineSegment(sketch, "E26.6.45.0", {"start": v(20.25, 0.25) * mm, "end": v(20.25, 9.75) * mm});
            skLineSegment(sketch, "E26.9.45.0", {"start": v(20.5, 9.75) * mm, "end": v(20.5, 0.25) * mm});
            skLineSegment(sketch, "E26.12.45.0", {"start": v(20.25, 9.75) * mm, "end": v(20.5, 9.75) * mm});
            skLineSegment(sketch, "E26.15.45.0", {"start": v(19.75, 4) * mm, "end": v(20, 4) * mm});
            skLineSegment(sketch, "E26.18.45.0", {"start": v(20.5, 0.25) * mm, "end": v(20.25, 0.25) * mm});
            skLineSegment(sketch, "E26.21.45.0", {"start": v(19.75, 3.5) * mm, "end": v(19.75, 0) * mm});
            skLineSegment(sketch, "E26.24.45.0", {"start": v(20, 3.5) * mm, "end": v(19.75, 3.5) * mm});
            skLineSegment(sketch, "E26.27.45.0", {"start": v(20, 0) * mm, "end": v(20, 3.5) * mm});
            skLineSegment(sketch, "E26.30.45.0", {"start": v(19.75, -3.5) * mm, "end": v(19.75, 0) * mm});
            skLineSegment(sketch, "E26.33.45.0", {"start": v(20, -3.5) * mm, "end": v(19.75, -3.5) * mm});
            skLineSegment(sketch, "E26.36.45.0", {"start": v(20, 0) * mm, "end": v(20, -3.5) * mm});
            skLineSegment(sketch, "E26.39.45.0", {"start": v(20.25, -0.25) * mm, "end": v(20.25, -9.75) * mm});
            skLineSegment(sketch, "E26.42.45.0", {"start": v(20.5, -0.25) * mm, "end": v(20.25, -0.25) * mm});
            skLineSegment(sketch, "E26.45.45.0", {"start": v(20.5, -9.75) * mm, "end": v(20.5, -0.25) * mm});
            skLineSegment(sketch, "E26.48.45.0", {"start": v(20.25, -9.75) * mm, "end": v(20.5, -9.75) * mm});
            skLineSegment(sketch, "E26.51.45.0", {"start": v(20, -4) * mm, "end": v(20, -10) * mm});
            skLineSegment(sketch, "E26.54.45.0", {"start": v(19.75, -10) * mm, "end": v(19.75, -4) * mm});
            skLineSegment(sketch, "E26.57.45.0", {"start": v(19.75, -4) * mm, "end": v(20, -4) * mm});
            skLineSegment(sketch, "E26.0.46.0", {"start": v(20.75, 10) * mm, "end": v(20.75, 4) * mm});
            skLineSegment(sketch, "E26.3.46.0", {"start": v(21, 4) * mm, "end": v(21, 10) * mm});
            skLineSegment(sketch, "E26.6.46.0", {"start": v(21.25, 0.25) * mm, "end": v(21.25, 9.75) * mm});
            skLineSegment(sketch, "E26.9.46.0", {"start": v(21.5, 9.75) * mm, "end": v(21.5, 0.25) * mm});
            skLineSegment(sketch, "E26.12.46.0", {"start": v(21.25, 9.75) * mm, "end": v(21.5, 9.75) * mm});
            skLineSegment(sketch, "E26.15.46.0", {"start": v(20.75, 4) * mm, "end": v(21, 4) * mm});
            skLineSegment(sketch, "E26.18.46.0", {"start": v(21.5, 0.25) * mm, "end": v(21.25, 0.25) * mm});
            skLineSegment(sketch, "E26.21.46.0", {"start": v(20.75, 3.5) * mm, "end": v(20.75, 0) * mm});
            skLineSegment(sketch, "E26.24.46.0", {"start": v(21, 3.5) * mm, "end": v(20.75, 3.5) * mm});
            skLineSegment(sketch, "E26.27.46.0", {"start": v(21, 0) * mm, "end": v(21, 3.5) * mm});
            skLineSegment(sketch, "E26.30.46.0", {"start": v(20.75, -3.5) * mm, "end": v(20.75, 0) * mm});
            skLineSegment(sketch, "E26.33.46.0", {"start": v(21, -3.5) * mm, "end": v(20.75, -3.5) * mm});
            skLineSegment(sketch, "E26.36.46.0", {"start": v(21, 0) * mm, "end": v(21, -3.5) * mm});
            skLineSegment(sketch, "E26.39.46.0", {"start": v(21.25, -0.25) * mm, "end": v(21.25, -9.75) * mm});
            skLineSegment(sketch, "E26.42.46.0", {"start": v(21.5, -0.25) * mm, "end": v(21.25, -0.25) * mm});
            skLineSegment(sketch, "E26.45.46.0", {"start": v(21.5, -9.75) * mm, "end": v(21.5, -0.25) * mm});
            skLineSegment(sketch, "E26.48.46.0", {"start": v(21.25, -9.75) * mm, "end": v(21.5, -9.75) * mm});
            skLineSegment(sketch, "E26.51.46.0", {"start": v(21, -4) * mm, "end": v(21, -10) * mm});
            skLineSegment(sketch, "E26.54.46.0", {"start": v(20.75, -10) * mm, "end": v(20.75, -4) * mm});
            skLineSegment(sketch, "E26.57.46.0", {"start": v(20.75, -4) * mm, "end": v(21, -4) * mm});
            skLineSegment(sketch, "E26.0.47.0", {"start": v(21.75, 10) * mm, "end": v(21.75, 4) * mm});
            skLineSegment(sketch, "E26.3.47.0", {"start": v(22, 4) * mm, "end": v(22, 10) * mm});
            skLineSegment(sketch, "E26.6.47.0", {"start": v(22.25, 0.25) * mm, "end": v(22.25, 9.75) * mm});
            skLineSegment(sketch, "E26.9.47.0", {"start": v(22.5, 9.75) * mm, "end": v(22.5, 0.25) * mm});
            skLineSegment(sketch, "E26.12.47.0", {"start": v(22.25, 9.75) * mm, "end": v(22.5, 9.75) * mm});
            skLineSegment(sketch, "E26.15.47.0", {"start": v(21.75, 4) * mm, "end": v(22, 4) * mm});
            skLineSegment(sketch, "E26.18.47.0", {"start": v(22.5, 0.25) * mm, "end": v(22.25, 0.25) * mm});
            skLineSegment(sketch, "E26.21.47.0", {"start": v(21.75, 3.5) * mm, "end": v(21.75, 0) * mm});
            skLineSegment(sketch, "E26.24.47.0", {"start": v(22, 3.5) * mm, "end": v(21.75, 3.5) * mm});
            skLineSegment(sketch, "E26.27.47.0", {"start": v(22, 0) * mm, "end": v(22, 3.5) * mm});
            skLineSegment(sketch, "E26.30.47.0", {"start": v(21.75, -3.5) * mm, "end": v(21.75, 0) * mm});
            skLineSegment(sketch, "E26.33.47.0", {"start": v(22, -3.5) * mm, "end": v(21.75, -3.5) * mm});
            skLineSegment(sketch, "E26.36.47.0", {"start": v(22, 0) * mm, "end": v(22, -3.5) * mm});
            skLineSegment(sketch, "E26.39.47.0", {"start": v(22.25, -0.25) * mm, "end": v(22.25, -9.75) * mm});
            skLineSegment(sketch, "E26.42.47.0", {"start": v(22.5, -0.25) * mm, "end": v(22.25, -0.25) * mm});
            skLineSegment(sketch, "E26.45.47.0", {"start": v(22.5, -9.75) * mm, "end": v(22.5, -0.25) * mm});
            skLineSegment(sketch, "E26.48.47.0", {"start": v(22.25, -9.75) * mm, "end": v(22.5, -9.75) * mm});
            skLineSegment(sketch, "E26.51.47.0", {"start": v(22, -4) * mm, "end": v(22, -10) * mm});
            skLineSegment(sketch, "E26.54.47.0", {"start": v(21.75, -10) * mm, "end": v(21.75, -4) * mm});
            skLineSegment(sketch, "E26.57.47.0", {"start": v(21.75, -4) * mm, "end": v(22, -4) * mm});
            skLineSegment(sketch, "E26.0.48.0", {"start": v(22.75, 10) * mm, "end": v(22.75, 4) * mm});
            skLineSegment(sketch, "E26.3.48.0", {"start": v(23, 4) * mm, "end": v(23, 10) * mm});
            skLineSegment(sketch, "E26.6.48.0", {"start": v(23.25, 0.25) * mm, "end": v(23.25, 9.75) * mm});
            skLineSegment(sketch, "E26.9.48.0", {"start": v(23.5, 9.75) * mm, "end": v(23.5, 0.25) * mm});
            skLineSegment(sketch, "E26.12.48.0", {"start": v(23.25, 9.75) * mm, "end": v(23.5, 9.75) * mm});
            skLineSegment(sketch, "E26.15.48.0", {"start": v(22.75, 4) * mm, "end": v(23, 4) * mm});
            skLineSegment(sketch, "E26.18.48.0", {"start": v(23.5, 0.25) * mm, "end": v(23.25, 0.25) * mm});
            skLineSegment(sketch, "E26.21.48.0", {"start": v(22.75, 3.5) * mm, "end": v(22.75, 0) * mm});
            skLineSegment(sketch, "E26.24.48.0", {"start": v(23, 3.5) * mm, "end": v(22.75, 3.5) * mm});
            skLineSegment(sketch, "E26.27.48.0", {"start": v(23, 0) * mm, "end": v(23, 3.5) * mm});
            skLineSegment(sketch, "E26.30.48.0", {"start": v(22.75, -3.5) * mm, "end": v(22.75, 0) * mm});
            skLineSegment(sketch, "E26.33.48.0", {"start": v(23, -3.5) * mm, "end": v(22.75, -3.5) * mm});
            skLineSegment(sketch, "E26.36.48.0", {"start": v(23, 0) * mm, "end": v(23, -3.5) * mm});
            skLineSegment(sketch, "E26.39.48.0", {"start": v(23.25, -0.25) * mm, "end": v(23.25, -9.75) * mm});
            skLineSegment(sketch, "E26.42.48.0", {"start": v(23.5, -0.25) * mm, "end": v(23.25, -0.25) * mm});
            skLineSegment(sketch, "E26.45.48.0", {"start": v(23.5, -9.75) * mm, "end": v(23.5, -0.25) * mm});
            skLineSegment(sketch, "E26.48.48.0", {"start": v(23.25, -9.75) * mm, "end": v(23.5, -9.75) * mm});
            skLineSegment(sketch, "E26.51.48.0", {"start": v(23, -4) * mm, "end": v(23, -10) * mm});
            skLineSegment(sketch, "E26.54.48.0", {"start": v(22.75, -10) * mm, "end": v(22.75, -4) * mm});
            skLineSegment(sketch, "E26.57.48.0", {"start": v(22.75, -4) * mm, "end": v(23, -4) * mm});
            skLineSegment(sketch, "E26.0.49.0", {"start": v(23.75, 10) * mm, "end": v(23.75, 4) * mm});
            skLineSegment(sketch, "E26.3.49.0", {"start": v(24, 4) * mm, "end": v(24, 10) * mm});
            skLineSegment(sketch, "E26.6.49.0", {"start": v(24.25, 0.25) * mm, "end": v(24.25, 9.75) * mm});
            skLineSegment(sketch, "E26.9.49.0", {"start": v(24.5, 9.75) * mm, "end": v(24.5, 0.25) * mm});
            skLineSegment(sketch, "E26.12.49.0", {"start": v(24.25, 9.75) * mm, "end": v(24.5, 9.75) * mm});
            skLineSegment(sketch, "E26.15.49.0", {"start": v(23.75, 4) * mm, "end": v(24, 4) * mm});
            skLineSegment(sketch, "E26.18.49.0", {"start": v(24.5, 0.25) * mm, "end": v(24.25, 0.25) * mm});
            skLineSegment(sketch, "E26.21.49.0", {"start": v(23.75, 3.5) * mm, "end": v(23.75, 0) * mm});
            skLineSegment(sketch, "E26.24.49.0", {"start": v(24, 3.5) * mm, "end": v(23.75, 3.5) * mm});
            skLineSegment(sketch, "E26.27.49.0", {"start": v(24, 0) * mm, "end": v(24, 3.5) * mm});
            skLineSegment(sketch, "E26.30.49.0", {"start": v(23.75, -3.5) * mm, "end": v(23.75, 0) * mm});
            skLineSegment(sketch, "E26.33.49.0", {"start": v(24, -3.5) * mm, "end": v(23.75, -3.5) * mm});
            skLineSegment(sketch, "E26.36.49.0", {"start": v(24, 0) * mm, "end": v(24, -3.5) * mm});
            skLineSegment(sketch, "E26.39.49.0", {"start": v(24.25, -0.25) * mm, "end": v(24.25, -9.75) * mm});
            skLineSegment(sketch, "E26.42.49.0", {"start": v(24.5, -0.25) * mm, "end": v(24.25, -0.25) * mm});
            skLineSegment(sketch, "E26.45.49.0", {"start": v(24.5, -9.75) * mm, "end": v(24.5, -0.25) * mm});
            skLineSegment(sketch, "E26.48.49.0", {"start": v(24.25, -9.75) * mm, "end": v(24.5, -9.75) * mm});
            skLineSegment(sketch, "E26.51.49.0", {"start": v(24, -4) * mm, "end": v(24, -10) * mm});
            skLineSegment(sketch, "E26.54.49.0", {"start": v(23.75, -10) * mm, "end": v(23.75, -4) * mm});
            skLineSegment(sketch, "E26.57.49.0", {"start": v(23.75, -4) * mm, "end": v(24, -4) * mm});
            skLineSegment(sketch, "E26.0.50.0", {"start": v(24.75, 10) * mm, "end": v(24.75, 4) * mm});
            skLineSegment(sketch, "E26.3.50.0", {"start": v(25, 4) * mm, "end": v(25, 10) * mm});
            skLineSegment(sketch, "E26.6.50.0", {"start": v(25.25, 0.25) * mm, "end": v(25.25, 9.75) * mm});
            skLineSegment(sketch, "E26.9.50.0", {"start": v(25.5, 9.75) * mm, "end": v(25.5, 0.25) * mm});
            skLineSegment(sketch, "E26.12.50.0", {"start": v(25.25, 9.75) * mm, "end": v(25.5, 9.75) * mm});
            skLineSegment(sketch, "E26.15.50.0", {"start": v(24.75, 4) * mm, "end": v(25, 4) * mm});
            skLineSegment(sketch, "E26.18.50.0", {"start": v(25.5, 0.25) * mm, "end": v(25.25, 0.25) * mm});
            skLineSegment(sketch, "E26.21.50.0", {"start": v(24.75, 3.5) * mm, "end": v(24.75, 0) * mm});
            skLineSegment(sketch, "E26.24.50.0", {"start": v(25, 3.5) * mm, "end": v(24.75, 3.5) * mm});
            skLineSegment(sketch, "E26.27.50.0", {"start": v(25, 0) * mm, "end": v(25, 3.5) * mm});
            skLineSegment(sketch, "E26.30.50.0", {"start": v(24.75, -3.5) * mm, "end": v(24.75, 0) * mm});
            skLineSegment(sketch, "E26.33.50.0", {"start": v(25, -3.5) * mm, "end": v(24.75, -3.5) * mm});
            skLineSegment(sketch, "E26.36.50.0", {"start": v(25, 0) * mm, "end": v(25, -3.5) * mm});
            skLineSegment(sketch, "E26.39.50.0", {"start": v(25.25, -0.25) * mm, "end": v(25.25, -9.75) * mm});
            skLineSegment(sketch, "E26.42.50.0", {"start": v(25.5, -0.25) * mm, "end": v(25.25, -0.25) * mm});
            skLineSegment(sketch, "E26.45.50.0", {"start": v(25.5, -9.75) * mm, "end": v(25.5, -0.25) * mm});
            skLineSegment(sketch, "E26.48.50.0", {"start": v(25.25, -9.75) * mm, "end": v(25.5, -9.75) * mm});
            skLineSegment(sketch, "E26.51.50.0", {"start": v(25, -4) * mm, "end": v(25, -10) * mm});
            skLineSegment(sketch, "E26.54.50.0", {"start": v(24.75, -10) * mm, "end": v(24.75, -4) * mm});
            skLineSegment(sketch, "E26.57.50.0", {"start": v(24.75, -4) * mm, "end": v(25, -4) * mm});
            skLineSegment(sketch, "E26.0.51.0", {"start": v(25.75, 10) * mm, "end": v(25.75, 4) * mm});
            skLineSegment(sketch, "E26.3.51.0", {"start": v(26, 4) * mm, "end": v(26, 10) * mm});
            skLineSegment(sketch, "E26.6.51.0", {"start": v(26.25, 0.25) * mm, "end": v(26.25, 9.75) * mm});
            skLineSegment(sketch, "E26.9.51.0", {"start": v(26.5, 9.75) * mm, "end": v(26.5, 0.25) * mm});
            skLineSegment(sketch, "E26.12.51.0", {"start": v(26.25, 9.75) * mm, "end": v(26.5, 9.75) * mm});
            skLineSegment(sketch, "E26.15.51.0", {"start": v(25.75, 4) * mm, "end": v(26, 4) * mm});
            skLineSegment(sketch, "E26.18.51.0", {"start": v(26.5, 0.25) * mm, "end": v(26.25, 0.25) * mm});
            skLineSegment(sketch, "E26.21.51.0", {"start": v(25.75, 3.5) * mm, "end": v(25.75, 0) * mm});
            skLineSegment(sketch, "E26.24.51.0", {"start": v(26, 3.5) * mm, "end": v(25.75, 3.5) * mm});
            skLineSegment(sketch, "E26.27.51.0", {"start": v(26, 0) * mm, "end": v(26, 3.5) * mm});
            skLineSegment(sketch, "E26.30.51.0", {"start": v(25.75, -3.5) * mm, "end": v(25.75, 0) * mm});
            skLineSegment(sketch, "E26.33.51.0", {"start": v(26, -3.5) * mm, "end": v(25.75, -3.5) * mm});
            skLineSegment(sketch, "E26.36.51.0", {"start": v(26, 0) * mm, "end": v(26, -3.5) * mm});
            skLineSegment(sketch, "E26.39.51.0", {"start": v(26.25, -0.25) * mm, "end": v(26.25, -9.75) * mm});
            skLineSegment(sketch, "E26.42.51.0", {"start": v(26.5, -0.25) * mm, "end": v(26.25, -0.25) * mm});
            skLineSegment(sketch, "E26.45.51.0", {"start": v(26.5, -9.75) * mm, "end": v(26.5, -0.25) * mm});
            skLineSegment(sketch, "E26.48.51.0", {"start": v(26.25, -9.75) * mm, "end": v(26.5, -9.75) * mm});
            skLineSegment(sketch, "E26.51.51.0", {"start": v(26, -4) * mm, "end": v(26, -10) * mm});
            skLineSegment(sketch, "E26.54.51.0", {"start": v(25.75, -10) * mm, "end": v(25.75, -4) * mm});
            skLineSegment(sketch, "E26.57.51.0", {"start": v(25.75, -4) * mm, "end": v(26, -4) * mm});
            skSolve(sketch);
        }
        {
            var Q0;
            {var subQ39=sQuery(id+"F0.wireOp",EDGE,"E0.left");Q0=makeQuery(id+"F0.imprint","IMPRINT",FACE,{"disambiguationData":[TD([[makeQuery(id+"F0.imprint","IMPRINT",EDGE,{"derivedFrom":subQ39}),1.0]])]});}
            extrude(context, id + "F1", {"entities" : qUnion([Q0]), "depth" : 0.5 * mm});
        }
    });
